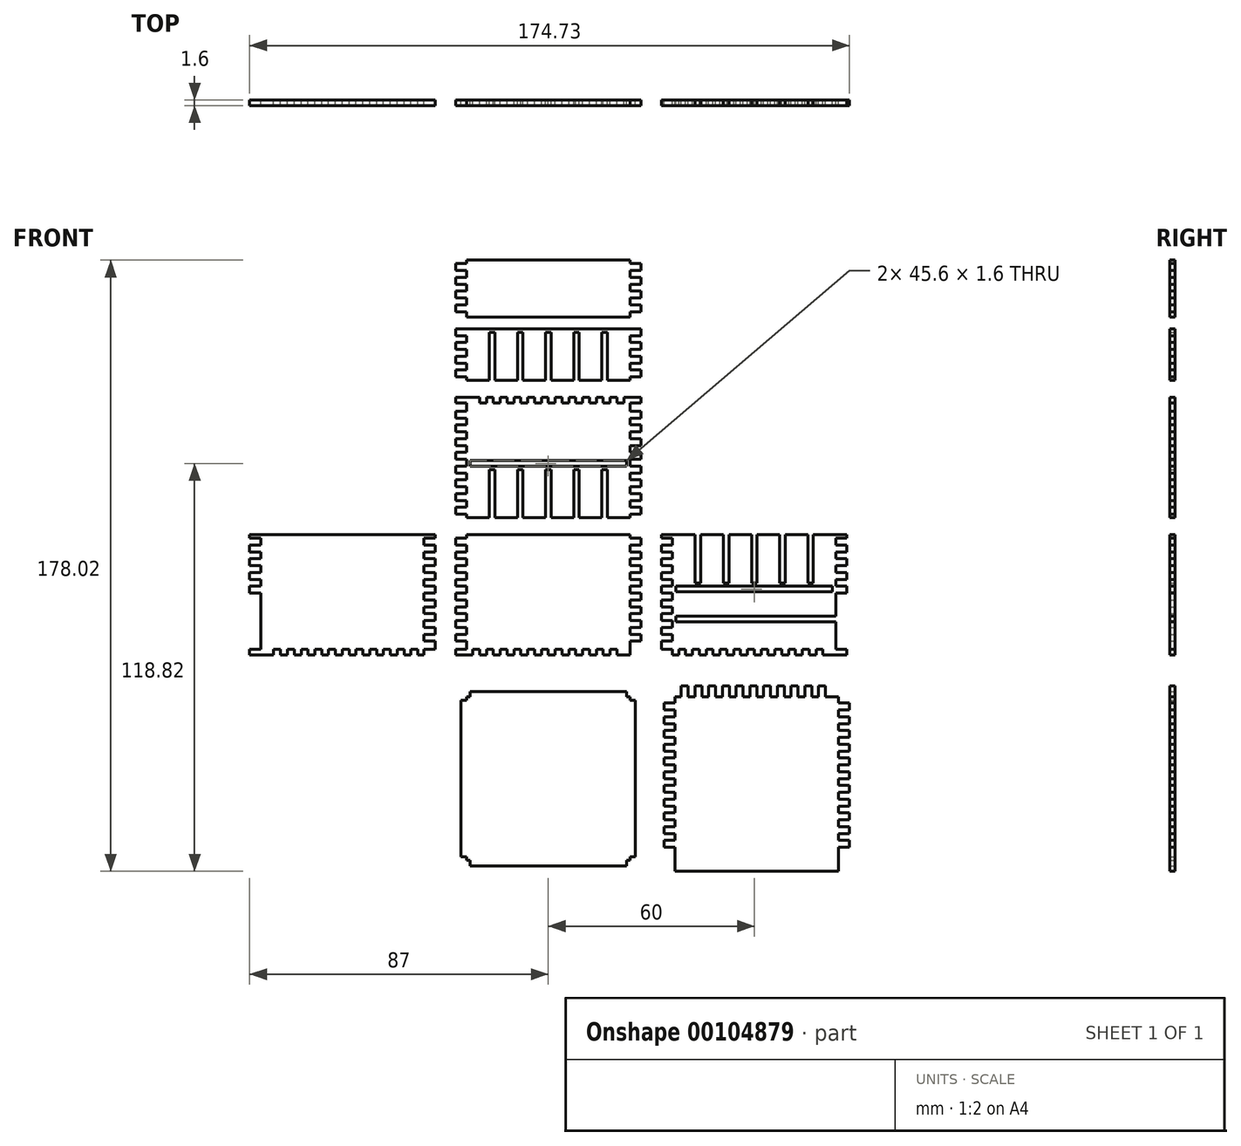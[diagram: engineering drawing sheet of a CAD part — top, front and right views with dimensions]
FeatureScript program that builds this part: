
annotation { "Feature Type Name" : "Feature", "Feature Type Description" : "" }
export const myFeature = defineFeature(function(context is Context, id is Id, definition is map)
    precondition{}
    {
        {
            var Q0;
            Q0=qCreatedBy(makeId("Front.planeOp"),FACE);
            var sketch = newSketch(context, id + "F0", { "sketchPlane" : qUnion([Q0])});
            skLineSegment(sketch, "E0", {"start": v(0, 17.5) * mm, "end": v(27, 17.5) * mm});
            skLineSegment(sketch, "E1", {"start": v(27, 17.5) * mm, "end": v(27, -17.5) * mm});
            skLineSegment(sketch, "E2", {"start": v(27, -17.5) * mm, "end": v(0, -17.5) * mm});
            skLineSegment(sketch, "E3", {"start": v(23.8, 17.5) * mm, "end": v(23.8, -17.5) * mm});
            skLineSegment(sketch, "E4", {"start": v(23.8, 16.5) * mm, "end": v(27, 16.5) * mm});
            skLineSegment(sketch, "E5", {"start": v(23.8, 14.5) * mm, "end": v(27, 14.5) * mm});
            skLineSegment(sketch, "E6.1.0.0", {"start": v(23.8, 12.5) * mm, "end": v(27, 12.5) * mm});
            skLineSegment(sketch, "E6.1.0.1", {"start": v(23.8, 10.5) * mm, "end": v(27, 10.5) * mm});
            skLineSegment(sketch, "E6.2.0.0", {"start": v(23.8, 8.5) * mm, "end": v(27, 8.5) * mm});
            skLineSegment(sketch, "E6.2.0.1", {"start": v(23.8, 6.5) * mm, "end": v(27, 6.5) * mm});
            skLineSegment(sketch, "E6.3.0.0", {"start": v(23.8, 4.5) * mm, "end": v(27, 4.5) * mm});
            skLineSegment(sketch, "E6.3.0.1", {"start": v(23.8, 2.5) * mm, "end": v(27, 2.5) * mm});
            skLineSegment(sketch, "E6.4.0.0", {"start": v(23.8, 0.5) * mm, "end": v(27, 0.5) * mm});
            skLineSegment(sketch, "E6.4.0.1", {"start": v(23.8, -1.5) * mm, "end": v(27, -1.5) * mm});
            skLineSegment(sketch, "E6.5.0.0", {"start": v(23.8, -3.5) * mm, "end": v(27, -3.5) * mm});
            skLineSegment(sketch, "E6.5.0.1", {"start": v(23.8, -5.5) * mm, "end": v(27, -5.5) * mm});
            skLineSegment(sketch, "E6.6.0.0", {"start": v(23.8, -7.5) * mm, "end": v(27, -7.5) * mm});
            skLineSegment(sketch, "E6.6.0.1", {"start": v(23.8, -9.5) * mm, "end": v(27, -9.5) * mm});
            skLineSegment(sketch, "E6.7.0.0", {"start": v(23.8, -11.5) * mm, "end": v(27, -11.5) * mm});
            skLineSegment(sketch, "E6.7.0.1", {"start": v(23.8, -13.5) * mm, "end": v(27, -13.5) * mm});
            skLineSegment(sketch, "E6.8.0.1", {"start": v(23.8, -17.5) * mm, "end": v(27, -17.5) * mm});
            skLineSegment(sketch, "E6.direction1", {"start": v(23.8, 16.5) * mm, "end": v(23.8, 12.5) * mm, "construction": true});
            skLineSegment(sketch, "E7.MirrorCS", {"start": v(0, 17.5) * mm, "end": v(-27, 17.5) * mm});
            skLineSegment(sketch, "E8.MirrorCS", {"start": v(-23.8, 16.5) * mm, "end": v(-27, 16.5) * mm});
            skLineSegment(sketch, "E9.MirrorCS", {"start": v(-23.8, 14.5) * mm, "end": v(-27, 14.5) * mm});
            skLineSegment(sketch, "E10.MirrorCS", {"start": v(-23.8, 12.5) * mm, "end": v(-27, 12.5) * mm});
            skLineSegment(sketch, "E11.MirrorCS", {"start": v(-23.8, 10.5) * mm, "end": v(-27, 10.5) * mm});
            skLineSegment(sketch, "E12.MirrorCS", {"start": v(-23.8, 8.5) * mm, "end": v(-27, 8.5) * mm});
            skLineSegment(sketch, "E13.MirrorCS", {"start": v(-23.8, 6.5) * mm, "end": v(-27, 6.5) * mm});
            skLineSegment(sketch, "E14.MirrorCS", {"start": v(-23.8, 4.5) * mm, "end": v(-27, 4.5) * mm});
            skLineSegment(sketch, "E15.MirrorCS", {"start": v(-23.8, 2.5) * mm, "end": v(-27, 2.5) * mm});
            skLineSegment(sketch, "E16.MirrorCS", {"start": v(-23.8, 0.5) * mm, "end": v(-27, 0.5) * mm});
            skLineSegment(sketch, "E17.MirrorCS", {"start": v(-23.8, -1.5) * mm, "end": v(-27, -1.5) * mm});
            skLineSegment(sketch, "E18.MirrorCS", {"start": v(-23.8, -5.5) * mm, "end": v(-27, -5.5) * mm});
            skLineSegment(sketch, "E19.MirrorCS", {"start": v(-23.8, -3.5) * mm, "end": v(-27, -3.5) * mm});
            skLineSegment(sketch, "E20.MirrorCS", {"start": v(-23.8, -7.5) * mm, "end": v(-27, -7.5) * mm});
            skLineSegment(sketch, "E21.MirrorCS", {"start": v(-23.8, -9.5) * mm, "end": v(-27, -9.5) * mm});
            skLineSegment(sketch, "E22.MirrorCS", {"start": v(-23.8, -11.5) * mm, "end": v(-27, -11.5) * mm});
            skLineSegment(sketch, "E23.MirrorCS", {"start": v(-23.8, -13.5) * mm, "end": v(-27, -13.5) * mm});
            skLineSegment(sketch, "E24.MirrorCS", {"start": v(-23.8, -17.5) * mm, "end": v(-27, -17.5) * mm});
            skLineSegment(sketch, "E25.MirrorCS", {"start": v(-27, -17.5) * mm, "end": v(0, -17.5) * mm});
            skLineSegment(sketch, "E26.MirrorCS", {"start": v(-23.8, 17.5) * mm, "end": v(-23.8, -17.5) * mm});
            skLineSegment(sketch, "E27.MirrorCS", {"start": v(-27, 17.5) * mm, "end": v(-27, -17.5) * mm});
            skLineSegment(sketch, "E28.1", {"start": v(-30, 20) * mm, "end": v(-30, -20) * mm, "construction": true});
            skLineSegment(sketch, "E28.5", {"start": v(30, 20) * mm, "end": v(30, -20) * mm, "construction": true});
            skLineSegment(sketch, "E29", {"start": v(-30, 20) * mm, "end": v(30, 20) * mm, "construction": true});
            skLineSegment(sketch, "E30", {"start": v(30, -20) * mm, "end": v(-30, -20) * mm, "construction": true});
            skLineSegment(sketch, "E31.MirrorCS", {"start": v(-0.8, 22.5) * mm, "end": v(-7.4, 22.5) * mm});
            skLineSegment(sketch, "E32.MirrorCS", {"start": v(0.8, 22.5) * mm, "end": v(7.4, 22.5) * mm});
            skLineSegment(sketch, "E33.MirrorCS", {"start": v(23.8, 23.5) * mm, "end": v(27, 23.5) * mm});
            skLineSegment(sketch, "E34.MirrorCS", {"start": v(23.8, 25.5) * mm, "end": v(27, 25.5) * mm});
            skLineSegment(sketch, "E35.MirrorCS", {"start": v(23.8, 27.5) * mm, "end": v(27, 27.5) * mm});
            skLineSegment(sketch, "E36.MirrorCS", {"start": v(23.8, 29.5) * mm, "end": v(27, 29.5) * mm});
            skLineSegment(sketch, "E37.MirrorCS", {"start": v(23.8, 31.5) * mm, "end": v(27, 31.5) * mm});
            skLineSegment(sketch, "E38.MirrorCS", {"start": v(23.8, 33.5) * mm, "end": v(27, 33.5) * mm});
            skLineSegment(sketch, "E39.MirrorCS", {"start": v(23.8, 35.5) * mm, "end": v(27, 35.5) * mm});
            skLineSegment(sketch, "E40.MirrorCS", {"start": v(23.8, 37.5) * mm, "end": v(27, 37.5) * mm});
            skLineSegment(sketch, "E41.MirrorCS", {"start": v(23.8, 39.5) * mm, "end": v(27, 39.5) * mm});
            skLineSegment(sketch, "E42.MirrorCS", {"start": v(23.8, 43.5) * mm, "end": v(27, 43.5) * mm});
            skLineSegment(sketch, "E43.MirrorCS", {"start": v(23.8, 45.5) * mm, "end": v(27, 45.5) * mm});
            skLineSegment(sketch, "E44.MirrorCS", {"start": v(23.8, 47.5) * mm, "end": v(27, 47.5) * mm});
            skLineSegment(sketch, "E45.MirrorCS", {"start": v(23.8, 49.5) * mm, "end": v(27, 49.5) * mm});
            skLineSegment(sketch, "E46.MirrorCS", {"start": v(23.8, 51.5) * mm, "end": v(27, 51.5) * mm});
            skLineSegment(sketch, "E47.MirrorCS", {"start": v(23.8, 53.5) * mm, "end": v(27, 53.5) * mm});
            skLineSegment(sketch, "E48.MirrorCS", {"start": v(27, 57.5) * mm, "end": v(0, 57.5) * mm});
            skLineSegment(sketch, "E49.MirrorCS", {"start": v(-27, 57.5) * mm, "end": v(0, 57.5) * mm});
            skLineSegment(sketch, "E50.MirrorCS", {"start": v(-23.8, 53.5) * mm, "end": v(-27, 53.5) * mm});
            skLineSegment(sketch, "E51.MirrorCS", {"start": v(-23.8, 51.5) * mm, "end": v(-27, 51.5) * mm});
            skLineSegment(sketch, "E52.MirrorCS", {"start": v(-23.8, 49.5) * mm, "end": v(-27, 49.5) * mm});
            skLineSegment(sketch, "E53.MirrorCS", {"start": v(-23.8, 47.5) * mm, "end": v(-27, 47.5) * mm});
            skLineSegment(sketch, "E54.MirrorCS", {"start": v(-23.8, 45.5) * mm, "end": v(-27, 45.5) * mm});
            skLineSegment(sketch, "E55.MirrorCS", {"start": v(-23.8, 43.5) * mm, "end": v(-27, 43.5) * mm});
            skLineSegment(sketch, "E56.MirrorCS", {"start": v(-23.8, 39.5) * mm, "end": v(-27, 39.5) * mm});
            skLineSegment(sketch, "E57.MirrorCS", {"start": v(-23.8, 37.5) * mm, "end": v(-27, 37.5) * mm});
            skLineSegment(sketch, "E58.MirrorCS", {"start": v(-23.8, 35.5) * mm, "end": v(-27, 35.5) * mm});
            skLineSegment(sketch, "E59.MirrorCS", {"start": v(-23.8, 33.5) * mm, "end": v(-27, 33.5) * mm});
            skLineSegment(sketch, "E60.MirrorCS", {"start": v(-23.8, 31.5) * mm, "end": v(-27, 31.5) * mm});
            skLineSegment(sketch, "E61.MirrorCS", {"start": v(-23.8, 29.5) * mm, "end": v(-27, 29.5) * mm});
            skLineSegment(sketch, "E62.MirrorCS", {"start": v(-23.8, 27.5) * mm, "end": v(-27, 27.5) * mm});
            skLineSegment(sketch, "E63.MirrorCS", {"start": v(-23.8, 25.5) * mm, "end": v(-27, 25.5) * mm});
            skLineSegment(sketch, "E64.MirrorCS", {"start": v(-23.8, 23.5) * mm, "end": v(-27, 23.5) * mm});
            skLineSegment(sketch, "E65.MirrorCS", {"start": v(-27, 22.5) * mm, "end": v(-27, 57.5) * mm});
            skLineSegment(sketch, "E66.MirrorCS", {"start": v(-23.8, 22.5) * mm, "end": v(-23.8, 57.5) * mm});
            skLineSegment(sketch, "E67.MirrorCS", {"start": v(23.8, 22.5) * mm, "end": v(23.8, 57.5) * mm});
            skLineSegment(sketch, "E68.MirrorCS", {"start": v(27, 22.5) * mm, "end": v(27, 57.5) * mm});
            skLineSegment(sketch, "E69.MirrorCS", {"start": v(-60, 17.5) * mm, "end": v(-33, 17.5) * mm});
            skLineSegment(sketch, "E70.MirrorCS", {"start": v(-60, 17.5) * mm, "end": v(-87, 17.5) * mm});
            skLineSegment(sketch, "E71.MirrorCS", {"start": v(-33, -17.5) * mm, "end": v(-60, -17.5) * mm});
            skLineSegment(sketch, "E72.MirrorCS", {"start": v(-87, -17.5) * mm, "end": v(-60, -17.5) * mm});
            skLineSegment(sketch, "E73.MirrorCS", {"start": v(-36.2, -13.5) * mm, "end": v(-33, -13.5) * mm});
            skLineSegment(sketch, "E74.MirrorCS", {"start": v(-36.2, -11.5) * mm, "end": v(-33, -11.5) * mm});
            skLineSegment(sketch, "E75.MirrorCS", {"start": v(-36.2, -9.5) * mm, "end": v(-33, -9.5) * mm});
            skLineSegment(sketch, "E76.MirrorCS", {"start": v(-36.2, -7.5) * mm, "end": v(-33, -7.5) * mm});
            skLineSegment(sketch, "E77.MirrorCS", {"start": v(-36.2, -5.5) * mm, "end": v(-33, -5.5) * mm});
            skLineSegment(sketch, "E78.MirrorCS", {"start": v(-36.2, -3.5) * mm, "end": v(-33, -3.5) * mm});
            skLineSegment(sketch, "E79.MirrorCS", {"start": v(-36.2, -1.5) * mm, "end": v(-33, -1.5) * mm});
            skLineSegment(sketch, "E80.MirrorCS", {"start": v(-36.2, 0.5) * mm, "end": v(-33, 0.5) * mm});
            skLineSegment(sketch, "E81.MirrorCS", {"start": v(-36.2, 2.5) * mm, "end": v(-33, 2.5) * mm});
            skLineSegment(sketch, "E82.MirrorCS", {"start": v(-36.2, 4.5) * mm, "end": v(-33, 4.5) * mm});
            skLineSegment(sketch, "E83.MirrorCS", {"start": v(-36.2, 6.5) * mm, "end": v(-33, 6.5) * mm});
            skLineSegment(sketch, "E84.MirrorCS", {"start": v(-36.2, 8.5) * mm, "end": v(-33, 8.5) * mm});
            skLineSegment(sketch, "E85.MirrorCS", {"start": v(-36.2, 10.5) * mm, "end": v(-33, 10.5) * mm});
            skLineSegment(sketch, "E86.MirrorCS", {"start": v(-36.2, 12.5) * mm, "end": v(-33, 12.5) * mm});
            skLineSegment(sketch, "E87.MirrorCS", {"start": v(-36.2, 14.5) * mm, "end": v(-33, 14.5) * mm});
            skLineSegment(sketch, "E88.MirrorCS", {"start": v(-36.2, 16.5) * mm, "end": v(-33, 16.5) * mm});
            skLineSegment(sketch, "E89.MirrorCS", {"start": v(-36.2, 17.5) * mm, "end": v(-36.2, -17.5) * mm});
            skLineSegment(sketch, "E90.MirrorCS", {"start": v(-33, 17.5) * mm, "end": v(-33, -17.5) * mm});
            skLineSegment(sketch, "E91.MirrorCS", {"start": v(-83.8, 17.5) * mm, "end": v(-83.8, -17.5) * mm});
            skLineSegment(sketch, "E92.MirrorCS", {"start": v(-87, 17.5) * mm, "end": v(-87, -17.5) * mm});
            skLineSegment(sketch, "E93.MirrorCS", {"start": v(-83.8, 16.5) * mm, "end": v(-87, 16.5) * mm});
            skLineSegment(sketch, "E94.MirrorCS", {"start": v(-83.8, 14.5) * mm, "end": v(-87, 14.5) * mm});
            skLineSegment(sketch, "E95.MirrorCS", {"start": v(-83.8, 12.5) * mm, "end": v(-87, 12.5) * mm});
            skLineSegment(sketch, "E96.MirrorCS", {"start": v(-83.8, 10.5) * mm, "end": v(-87, 10.5) * mm});
            skLineSegment(sketch, "E97.MirrorCS", {"start": v(-83.8, 8.5) * mm, "end": v(-87, 8.5) * mm});
            skLineSegment(sketch, "E98.MirrorCS", {"start": v(-83.8, 6.5) * mm, "end": v(-87, 6.5) * mm});
            skLineSegment(sketch, "E99.MirrorCS", {"start": v(-83.8, 4.5) * mm, "end": v(-87, 4.5) * mm});
            skLineSegment(sketch, "E100.MirrorCS", {"start": v(-83.8, 2.5) * mm, "end": v(-87, 2.5) * mm});
            skLineSegment(sketch, "E101.MirrorCS", {"start": v(-83.8, 0.5) * mm, "end": v(-87, 0.5) * mm});
            skLineSegment(sketch, "E102.MirrorCS", {"start": v(30, 60) * mm, "end": v(-30, 60) * mm, "construction": true});
            skLineSegment(sketch, "E103.MirrorCS", {"start": v(27, 62.5) * mm, "end": v(17.2, 62.5) * mm});
            skLineSegment(sketch, "E104.MirrorCS", {"start": v(-27, 62.5) * mm, "end": v(-17.2, 62.5) * mm});
            skLineSegment(sketch, "E105.MirrorCS", {"start": v(0, 97.5) * mm, "end": v(-27, 97.5) * mm});
            skLineSegment(sketch, "E106.MirrorCS", {"start": v(0, 97.5) * mm, "end": v(27, 97.5) * mm});
            skLineSegment(sketch, "E107.MirrorCS", {"start": v(-23.8, 96.5) * mm, "end": v(-27, 96.5) * mm});
            skLineSegment(sketch, "E108.MirrorCS", {"start": v(-23.8, 94.5) * mm, "end": v(-27, 94.5) * mm});
            skLineSegment(sketch, "E109.MirrorCS", {"start": v(-23.8, 92.5) * mm, "end": v(-27, 92.5) * mm});
            skLineSegment(sketch, "E110.MirrorCS", {"start": v(-23.8, 90.5) * mm, "end": v(-27, 90.5) * mm});
            skLineSegment(sketch, "E111.MirrorCS", {"start": v(-23.8, 88.5) * mm, "end": v(-27, 88.5) * mm});
            skLineSegment(sketch, "E112.MirrorCS", {"start": v(-23.8, 86.5) * mm, "end": v(-27, 86.5) * mm});
            skLineSegment(sketch, "E113.MirrorCS", {"start": v(-23.8, 84.5) * mm, "end": v(-27, 84.5) * mm});
            skLineSegment(sketch, "E114.MirrorCS", {"start": v(-23.8, 82.5) * mm, "end": v(-27, 82.5) * mm});
            skLineSegment(sketch, "E115.MirrorCS", {"start": v(23.8, 82.5) * mm, "end": v(27, 82.5) * mm});
            skLineSegment(sketch, "E116.MirrorCS", {"start": v(23.8, 84.5) * mm, "end": v(27, 84.5) * mm});
            skLineSegment(sketch, "E117.MirrorCS", {"start": v(23.8, 96.5) * mm, "end": v(27, 96.5) * mm});
            skLineSegment(sketch, "E118.MirrorCS", {"start": v(23.8, 94.5) * mm, "end": v(27, 94.5) * mm});
            skLineSegment(sketch, "E119.MirrorCS", {"start": v(23.8, 92.5) * mm, "end": v(27, 92.5) * mm});
            skLineSegment(sketch, "E120.MirrorCS", {"start": v(23.8, 90.5) * mm, "end": v(27, 90.5) * mm});
            skLineSegment(sketch, "E121.MirrorCS", {"start": v(23.8, 88.5) * mm, "end": v(27, 88.5) * mm});
            skLineSegment(sketch, "E122.MirrorCS", {"start": v(23.8, 86.5) * mm, "end": v(27, 86.5) * mm});
            skLineSegment(sketch, "E123.MirrorCS", {"start": v(23.8, 97.5) * mm, "end": v(23.8, 82.5) * mm});
            skLineSegment(sketch, "E124.MirrorCS", {"start": v(27, 97.5) * mm, "end": v(27, 82.5) * mm});
            skLineSegment(sketch, "E125.MirrorCS", {"start": v(-23.8, 97.5) * mm, "end": v(-23.8, 82.5) * mm});
            skLineSegment(sketch, "E126.MirrorCS", {"start": v(-27, 97.5) * mm, "end": v(-27, 82.5) * mm});
            skLineSegment(sketch, "E127", {"start": v(0, -15.9) * mm, "end": v(22, -15.9) * mm});
            skLineSegment(sketch, "E128", {"start": v(22, -15.9) * mm, "end": v(22, -17.5) * mm});
            skLineSegment(sketch, "E129", {"start": v(20, -15.9) * mm, "end": v(20, -17.5) * mm});
            skLineSegment(sketch, "E130.MirrorCS", {"start": v(0, -15.9) * mm, "end": v(-22, -15.9) * mm});
            skLineSegment(sketch, "E131.MirrorCS", {"start": v(-22, -15.9) * mm, "end": v(-22, -17.5) * mm});
            skLineSegment(sketch, "E132.MirrorCS", {"start": v(-20, -15.9) * mm, "end": v(-20, -17.5) * mm});
            skLineSegment(sketch, "E133.1.0.0", {"start": v(16, -15.9) * mm, "end": v(16, -17.5) * mm});
            skLineSegment(sketch, "E133.1.0.1", {"start": v(18, -15.9) * mm, "end": v(18, -17.5) * mm});
            skLineSegment(sketch, "E133.2.0.0", {"start": v(12, -15.9) * mm, "end": v(12, -17.5) * mm});
            skLineSegment(sketch, "E133.2.0.1", {"start": v(14, -15.9) * mm, "end": v(14, -17.5) * mm});
            skLineSegment(sketch, "E133.3.0.0", {"start": v(8, -15.9) * mm, "end": v(8, -17.5) * mm});
            skLineSegment(sketch, "E133.3.0.1", {"start": v(10, -15.9) * mm, "end": v(10, -17.5) * mm});
            skLineSegment(sketch, "E133.4.0.0", {"start": v(4, -15.9) * mm, "end": v(4, -17.5) * mm});
            skLineSegment(sketch, "E133.4.0.1", {"start": v(6, -15.9) * mm, "end": v(6, -17.5) * mm});
            skLineSegment(sketch, "E133.5.0.1", {"start": v(2, -15.9) * mm, "end": v(2, -17.5) * mm});
            skLineSegment(sketch, "E133.direction1", {"start": v(20, -17.5) * mm, "end": v(16, -17.5) * mm, "construction": true});
            skLineSegment(sketch, "E134.1.0.0", {"start": v(-16, -15.9) * mm, "end": v(-16, -17.5) * mm});
            skLineSegment(sketch, "E134.1.0.1", {"start": v(-18, -15.9) * mm, "end": v(-18, -17.5) * mm});
            skLineSegment(sketch, "E134.2.0.0", {"start": v(-12, -15.9) * mm, "end": v(-12, -17.5) * mm});
            skLineSegment(sketch, "E134.2.0.1", {"start": v(-14, -15.9) * mm, "end": v(-14, -17.5) * mm});
            skLineSegment(sketch, "E134.3.0.0", {"start": v(-8, -15.9) * mm, "end": v(-8, -17.5) * mm});
            skLineSegment(sketch, "E134.3.0.1", {"start": v(-10, -15.9) * mm, "end": v(-10, -17.5) * mm});
            skLineSegment(sketch, "E134.4.0.0", {"start": v(-4, -15.9) * mm, "end": v(-4, -17.5) * mm});
            skLineSegment(sketch, "E134.4.0.1", {"start": v(-6, -15.9) * mm, "end": v(-6, -17.5) * mm});
            skLineSegment(sketch, "E134.5.0.1", {"start": v(-2, -15.9) * mm, "end": v(-2, -17.5) * mm});
            skLineSegment(sketch, "E134.direction1", {"start": v(-22, -17.5) * mm, "end": v(-18, -17.5) * mm, "construction": true});
            skLineSegment(sketch, "E135", {"start": v(0, -15.9) * mm, "end": v(0, -17.5) * mm});
            skLineSegment(sketch, "E136.MirrorCS", {"start": v(59.2, 17.5) * mm, "end": v(52.6, 17.5) * mm});
            skLineSegment(sketch, "E137.MirrorCS", {"start": v(60.8, 17.5) * mm, "end": v(67.4, 17.5) * mm});
            skLineSegment(sketch, "E138.MirrorCS", {"start": v(33, 17.5) * mm, "end": v(33, -17.5) * mm});
            skLineSegment(sketch, "E139.MirrorCS", {"start": v(36.2, 17.5) * mm, "end": v(36.2, -17.5) * mm});
            skLineSegment(sketch, "E140.MirrorCS", {"start": v(83.8, 17.5) * mm, "end": v(83.8, -6.2) * mm});
            skLineSegment(sketch, "E141.MirrorCS", {"start": v(87, 17.5) * mm, "end": v(87, -17.5) * mm});
            skLineSegment(sketch, "E142.MirrorCS", {"start": v(36.2, 16.5) * mm, "end": v(33, 16.5) * mm});
            skLineSegment(sketch, "E143.MirrorCS", {"start": v(36.2, 14.5) * mm, "end": v(33, 14.5) * mm});
            skLineSegment(sketch, "E144.MirrorCS", {"start": v(36.2, 12.5) * mm, "end": v(33, 12.5) * mm});
            skLineSegment(sketch, "E145.MirrorCS", {"start": v(36.2, 10.5) * mm, "end": v(33, 10.5) * mm});
            skLineSegment(sketch, "E146.MirrorCS", {"start": v(36.2, 8.5) * mm, "end": v(33, 8.5) * mm});
            skLineSegment(sketch, "E147.MirrorCS", {"start": v(36.2, 6.5) * mm, "end": v(33, 6.5) * mm});
            skLineSegment(sketch, "E148.MirrorCS", {"start": v(36.2, 4.5) * mm, "end": v(33, 4.5) * mm});
            skLineSegment(sketch, "E149.MirrorCS", {"start": v(36.2, 2.5) * mm, "end": v(33, 2.5) * mm});
            skLineSegment(sketch, "E150.MirrorCS", {"start": v(36.2, 0.5) * mm, "end": v(33, 0.5) * mm});
            skLineSegment(sketch, "E151.MirrorCS", {"start": v(36.2, -1.5) * mm, "end": v(33, -1.5) * mm});
            skLineSegment(sketch, "E152.MirrorCS", {"start": v(36.2, -3.5) * mm, "end": v(33, -3.5) * mm});
            skLineSegment(sketch, "E153.MirrorCS", {"start": v(36.2, -5.5) * mm, "end": v(33, -5.5) * mm});
            skLineSegment(sketch, "E154.MirrorCS", {"start": v(36.2, -7.5) * mm, "end": v(33, -7.5) * mm});
            skLineSegment(sketch, "E155.MirrorCS", {"start": v(36.2, -9.5) * mm, "end": v(33, -9.5) * mm});
            skLineSegment(sketch, "E156.MirrorCS", {"start": v(36.2, -11.5) * mm, "end": v(33, -11.5) * mm});
            skLineSegment(sketch, "E157.MirrorCS", {"start": v(36.2, -13.5) * mm, "end": v(33, -13.5) * mm});
            skLineSegment(sketch, "E158.MirrorCS", {"start": v(83.8, 0.5) * mm, "end": v(87, 0.5) * mm});
            skLineSegment(sketch, "E159.MirrorCS", {"start": v(83.8, 2.5) * mm, "end": v(87, 2.5) * mm});
            skLineSegment(sketch, "E160.MirrorCS", {"start": v(83.8, 4.5) * mm, "end": v(87, 4.5) * mm});
            skLineSegment(sketch, "E161.MirrorCS", {"start": v(83.8, 6.5) * mm, "end": v(87, 6.5) * mm});
            skLineSegment(sketch, "E162.MirrorCS", {"start": v(83.8, 8.5) * mm, "end": v(87, 8.5) * mm});
            skLineSegment(sketch, "E163.MirrorCS", {"start": v(83.8, 10.5) * mm, "end": v(87, 10.5) * mm});
            skLineSegment(sketch, "E164.MirrorCS", {"start": v(83.8, 12.5) * mm, "end": v(87, 12.5) * mm});
            skLineSegment(sketch, "E165.MirrorCS", {"start": v(83.8, 14.5) * mm, "end": v(87, 14.5) * mm});
            skLineSegment(sketch, "E166.MirrorCS", {"start": v(83.8, 16.5) * mm, "end": v(87, 16.5) * mm});
            skLineSegment(sketch, "E167.MirrorCS", {"start": v(60, -15.9) * mm, "end": v(82, -15.9) * mm});
            skLineSegment(sketch, "E168.MirrorCS", {"start": v(60, -15.9) * mm, "end": v(38, -15.9) * mm});
            skLineSegment(sketch, "E169.MirrorCS", {"start": v(87, -17.5) * mm, "end": v(60, -17.5) * mm});
            skLineSegment(sketch, "E170.MirrorCS", {"start": v(33, -17.5) * mm, "end": v(60, -17.5) * mm});
            skLineSegment(sketch, "E171.MirrorCS", {"start": v(38, -15.9) * mm, "end": v(38, -17.5) * mm});
            skLineSegment(sketch, "E172.MirrorCS", {"start": v(40, -15.9) * mm, "end": v(40, -17.5) * mm});
            skLineSegment(sketch, "E173.MirrorCS", {"start": v(42, -15.9) * mm, "end": v(42, -17.5) * mm});
            skLineSegment(sketch, "E174.MirrorCS", {"start": v(44, -15.9) * mm, "end": v(44, -17.5) * mm});
            skLineSegment(sketch, "E175.MirrorCS", {"start": v(46, -15.9) * mm, "end": v(46, -17.5) * mm});
            skLineSegment(sketch, "E176.MirrorCS", {"start": v(48, -15.9) * mm, "end": v(48, -17.5) * mm});
            skLineSegment(sketch, "E177.MirrorCS", {"start": v(50, -15.9) * mm, "end": v(50, -17.5) * mm});
            skLineSegment(sketch, "E178.MirrorCS", {"start": v(52, -15.9) * mm, "end": v(52, -17.5) * mm});
            skLineSegment(sketch, "E179.MirrorCS", {"start": v(54, -15.9) * mm, "end": v(54, -17.5) * mm});
            skLineSegment(sketch, "E180.MirrorCS", {"start": v(56, -15.9) * mm, "end": v(56, -17.5) * mm});
            skLineSegment(sketch, "E181.MirrorCS", {"start": v(58, -15.9) * mm, "end": v(58, -17.5) * mm});
            skLineSegment(sketch, "E182.MirrorCS", {"start": v(60, -15.9) * mm, "end": v(60, -17.5) * mm});
            skLineSegment(sketch, "E183.MirrorCS", {"start": v(62, -15.9) * mm, "end": v(62, -17.5) * mm});
            skLineSegment(sketch, "E184.MirrorCS", {"start": v(64, -15.9) * mm, "end": v(64, -17.5) * mm});
            skLineSegment(sketch, "E185.MirrorCS", {"start": v(66, -15.9) * mm, "end": v(66, -17.5) * mm});
            skLineSegment(sketch, "E186.MirrorCS", {"start": v(68, -15.9) * mm, "end": v(68, -17.5) * mm});
            skLineSegment(sketch, "E187.MirrorCS", {"start": v(70, -15.9) * mm, "end": v(70, -17.5) * mm});
            skLineSegment(sketch, "E188.MirrorCS", {"start": v(72, -15.9) * mm, "end": v(72, -17.5) * mm});
            skLineSegment(sketch, "E189.MirrorCS", {"start": v(74, -15.9) * mm, "end": v(74, -17.5) * mm});
            skLineSegment(sketch, "E190.MirrorCS", {"start": v(76, -15.9) * mm, "end": v(76, -17.5) * mm});
            skLineSegment(sketch, "E191.MirrorCS", {"start": v(78, -15.9) * mm, "end": v(78, -17.5) * mm});
            skLineSegment(sketch, "E192.MirrorCS", {"start": v(80, -15.9) * mm, "end": v(80, -17.5) * mm});
            skLineSegment(sketch, "E193.MirrorCS", {"start": v(82, -15.9) * mm, "end": v(82, -17.5) * mm});
            skLineSegment(sketch, "E194.MirrorCS", {"start": v(-60, -15.9) * mm, "end": v(-38, -15.9) * mm});
            skLineSegment(sketch, "E195.MirrorCS", {"start": v(-60, -15.9) * mm, "end": v(-82, -15.9) * mm});
            skLineSegment(sketch, "E196.MirrorCS", {"start": v(-38, -15.9) * mm, "end": v(-38, -17.5) * mm});
            skLineSegment(sketch, "E197.MirrorCS", {"start": v(-40, -15.9) * mm, "end": v(-40, -17.5) * mm});
            skLineSegment(sketch, "E198.MirrorCS", {"start": v(-42, -15.9) * mm, "end": v(-42, -17.5) * mm});
            skLineSegment(sketch, "E199.MirrorCS", {"start": v(-44, -15.9) * mm, "end": v(-44, -17.5) * mm});
            skLineSegment(sketch, "E200.MirrorCS", {"start": v(-46, -15.9) * mm, "end": v(-46, -17.5) * mm});
            skLineSegment(sketch, "E201.MirrorCS", {"start": v(-48, -15.9) * mm, "end": v(-48, -17.5) * mm});
            skLineSegment(sketch, "E202.MirrorCS", {"start": v(-50, -15.9) * mm, "end": v(-50, -17.5) * mm});
            skLineSegment(sketch, "E203.MirrorCS", {"start": v(-52, -15.9) * mm, "end": v(-52, -17.5) * mm});
            skLineSegment(sketch, "E204.MirrorCS", {"start": v(-54, -15.9) * mm, "end": v(-54, -17.5) * mm});
            skLineSegment(sketch, "E205.MirrorCS", {"start": v(-56, -15.9) * mm, "end": v(-56, -17.5) * mm});
            skLineSegment(sketch, "E206.MirrorCS", {"start": v(-58, -15.9) * mm, "end": v(-58, -17.5) * mm});
            skLineSegment(sketch, "E207.MirrorCS", {"start": v(-60, -15.9) * mm, "end": v(-60, -17.5) * mm});
            skLineSegment(sketch, "E208.MirrorCS", {"start": v(-62, -15.9) * mm, "end": v(-62, -17.5) * mm});
            skLineSegment(sketch, "E209.MirrorCS", {"start": v(-64, -15.9) * mm, "end": v(-64, -17.5) * mm});
            skLineSegment(sketch, "E210.MirrorCS", {"start": v(-82, -15.9) * mm, "end": v(-82, -17.5) * mm});
            skLineSegment(sketch, "E211.MirrorCS", {"start": v(-80, -15.9) * mm, "end": v(-80, -17.5) * mm});
            skLineSegment(sketch, "E212.MirrorCS", {"start": v(-78, -15.9) * mm, "end": v(-78, -17.5) * mm});
            skLineSegment(sketch, "E213.MirrorCS", {"start": v(-76, -15.9) * mm, "end": v(-76, -17.5) * mm});
            skLineSegment(sketch, "E214.MirrorCS", {"start": v(-74, -15.9) * mm, "end": v(-74, -17.5) * mm});
            skLineSegment(sketch, "E215.MirrorCS", {"start": v(-72, -15.9) * mm, "end": v(-72, -17.5) * mm});
            skLineSegment(sketch, "E216.MirrorCS", {"start": v(-70, -15.9) * mm, "end": v(-70, -17.5) * mm});
            skLineSegment(sketch, "E217.MirrorCS", {"start": v(-66, -15.9) * mm, "end": v(-66, -17.5) * mm});
            skLineSegment(sketch, "E218.MirrorCS", {"start": v(-68, -15.9) * mm, "end": v(-68, -17.5) * mm});
            skLineSegment(sketch, "E219.MirrorCS", {"start": v(0, 55.9) * mm, "end": v(-22, 55.9) * mm});
            skLineSegment(sketch, "E220.MirrorCS", {"start": v(0, 55.9) * mm, "end": v(22, 55.9) * mm});
            skLineSegment(sketch, "E221.MirrorCS", {"start": v(-22, 55.9) * mm, "end": v(-22, 57.5) * mm});
            skLineSegment(sketch, "E222.MirrorCS", {"start": v(-20, 55.9) * mm, "end": v(-20, 57.5) * mm});
            skLineSegment(sketch, "E223.MirrorCS", {"start": v(-18, 55.9) * mm, "end": v(-18, 57.5) * mm});
            skLineSegment(sketch, "E224.MirrorCS", {"start": v(-16, 55.9) * mm, "end": v(-16, 57.5) * mm});
            skLineSegment(sketch, "E225.MirrorCS", {"start": v(-14, 55.9) * mm, "end": v(-14, 57.5) * mm});
            skLineSegment(sketch, "E226.MirrorCS", {"start": v(-12, 55.9) * mm, "end": v(-12, 57.5) * mm});
            skLineSegment(sketch, "E227.MirrorCS", {"start": v(-10, 55.9) * mm, "end": v(-10, 57.5) * mm});
            skLineSegment(sketch, "E228.MirrorCS", {"start": v(-8, 55.9) * mm, "end": v(-8, 57.5) * mm});
            skLineSegment(sketch, "E229.MirrorCS", {"start": v(-6, 55.9) * mm, "end": v(-6, 57.5) * mm});
            skLineSegment(sketch, "E230.MirrorCS", {"start": v(-4, 55.9) * mm, "end": v(-4, 57.5) * mm});
            skLineSegment(sketch, "E231.MirrorCS", {"start": v(-2, 55.9) * mm, "end": v(-2, 57.5) * mm});
            skLineSegment(sketch, "E232.MirrorCS", {"start": v(0, 55.9) * mm, "end": v(0, 57.5) * mm});
            skLineSegment(sketch, "E233.MirrorCS", {"start": v(2, 55.9) * mm, "end": v(2, 57.5) * mm});
            skLineSegment(sketch, "E234.MirrorCS", {"start": v(4, 55.9) * mm, "end": v(4, 57.5) * mm});
            skLineSegment(sketch, "E235.MirrorCS", {"start": v(6, 55.9) * mm, "end": v(6, 57.5) * mm});
            skLineSegment(sketch, "E236.MirrorCS", {"start": v(8, 55.9) * mm, "end": v(8, 57.5) * mm});
            skLineSegment(sketch, "E237.MirrorCS", {"start": v(10, 55.9) * mm, "end": v(10, 57.5) * mm});
            skLineSegment(sketch, "E238.MirrorCS", {"start": v(12, 55.9) * mm, "end": v(12, 57.5) * mm});
            skLineSegment(sketch, "E239.MirrorCS", {"start": v(14, 55.9) * mm, "end": v(14, 57.5) * mm});
            skLineSegment(sketch, "E240.MirrorCS", {"start": v(16, 55.9) * mm, "end": v(16, 57.5) * mm});
            skLineSegment(sketch, "E241.MirrorCS", {"start": v(18, 55.9) * mm, "end": v(18, 57.5) * mm});
            skLineSegment(sketch, "E242.MirrorCS", {"start": v(20, 55.9) * mm, "end": v(20, 57.5) * mm});
            skLineSegment(sketch, "E243.MirrorCS", {"start": v(22, 55.9) * mm, "end": v(22, 57.5) * mm});
            skLineSegment(sketch, "E244", {"start": v(-23.8, -15.9) * mm, "end": v(-27, -15.9) * mm});
            skLineSegment(sketch, "E245", {"start": v(23.8, -15.9) * mm, "end": v(27, -15.9) * mm});
            skLineSegment(sketch, "E246", {"start": v(36.2, -15.9) * mm, "end": v(33, -15.9) * mm});
            skLineSegment(sketch, "E247", {"start": v(83.8, -15.9) * mm, "end": v(87, -15.9) * mm});
            skLineSegment(sketch, "E248", {"start": v(-36.2, -15.9) * mm, "end": v(-33, -15.9) * mm});
            skLineSegment(sketch, "E249", {"start": v(-83.8, -15.9) * mm, "end": v(-87, -15.9) * mm});
            skLineSegment(sketch, "E250", {"start": v(-23.8, 55.9) * mm, "end": v(-27, 55.9) * mm});
            skLineSegment(sketch, "E251", {"start": v(23.8, 55.9) * mm, "end": v(27, 55.9) * mm});
            skLineSegment(sketch, "E252.trimOffspring", {"start": v(-23.8, 77.5) * mm, "end": v(-23.8, 62.5) * mm});
            skLineSegment(sketch, "E253.trimOffspring", {"start": v(23.8, 77.5) * mm, "end": v(23.8, 62.5) * mm});
            skLineSegment(sketch, "E254.trimOffspring", {"start": v(27, 77.5) * mm, "end": v(27, 62.5) * mm});
            skLineSegment(sketch, "E255.trimOffspring", {"start": v(-27, 77.5) * mm, "end": v(-27, 62.5) * mm});
            skLineSegment(sketch, "E256", {"start": v(-23.8, 82.5) * mm, "end": v(-23.8, 80.9) * mm});
            skLineSegment(sketch, "E257", {"start": v(-23.8, 80.9) * mm, "end": v(23.8, 80.9) * mm});
            skLineSegment(sketch, "E258", {"start": v(23.8, 80.9) * mm, "end": v(23.8, 82.5) * mm});
            skLineSegment(sketch, "E259", {"start": v(-27, 63.5) * mm, "end": v(-23.8, 63.5) * mm});
            skLineSegment(sketch, "E260", {"start": v(-27, 65.5) * mm, "end": v(-23.8, 65.5) * mm});
            skLineSegment(sketch, "E261", {"start": v(-27, 67.5) * mm, "end": v(-23.8, 67.5) * mm});
            skLineSegment(sketch, "E262", {"start": v(27, 69.5) * mm, "end": v(23.8, 69.5) * mm});
            skLineSegment(sketch, "E263", {"start": v(-27, 71.5) * mm, "end": v(-23.8, 71.5) * mm});
            skLineSegment(sketch, "E264", {"start": v(-27, 73.5) * mm, "end": v(-23.8, 73.5) * mm});
            skLineSegment(sketch, "E265", {"start": v(-27, 75.5) * mm, "end": v(27, 75.5) * mm});
            skLineSegment(sketch, "E266", {"start": v(-27, 77.5) * mm, "end": v(27, 77.5) * mm});
            skLineSegment(sketch, "E267.trimOffspring", {"start": v(23.8, 63.5) * mm, "end": v(27, 63.5) * mm});
            skLineSegment(sketch, "E268.trimOffspring", {"start": v(23.8, 65.5) * mm, "end": v(27, 65.5) * mm});
            skLineSegment(sketch, "E269.trimOffspring", {"start": v(23.8, 67.5) * mm, "end": v(27, 67.5) * mm});
            skLineSegment(sketch, "E270.trimOffspring", {"start": v(-23.8, 69.5) * mm, "end": v(-27, 69.5) * mm});
            skLineSegment(sketch, "E271.trimOffspring", {"start": v(23.8, 71.5) * mm, "end": v(27, 71.5) * mm});
            skLineSegment(sketch, "E272.trimOffspring", {"start": v(23.8, 73.5) * mm, "end": v(27, 73.5) * mm});
            skLineSegment(sketch, "E273", {"start": v(-17.2, 62.5) * mm, "end": v(-17.2, 76.5) * mm});
            skLineSegment(sketch, "E274", {"start": v(-15.6, 62.5) * mm, "end": v(-15.6, 76.5) * mm});
            skLineSegment(sketch, "E275.1.0.0", {"start": v(-9, 62.5) * mm, "end": v(-9, 76.5) * mm});
            skLineSegment(sketch, "E275.1.0.1", {"start": v(-7.4, 62.5) * mm, "end": v(-7.4, 76.5) * mm});
            skLineSegment(sketch, "E275.2.0.0", {"start": v(-0.8, 62.5) * mm, "end": v(-0.8, 76.5) * mm});
            skLineSegment(sketch, "E275.2.0.1", {"start": v(0.8, 62.5) * mm, "end": v(0.8, 76.5) * mm});
            skLineSegment(sketch, "E275.3.0.0", {"start": v(7.4, 62.5) * mm, "end": v(7.4, 76.5) * mm});
            skLineSegment(sketch, "E275.3.0.1", {"start": v(9, 62.5) * mm, "end": v(9, 76.5) * mm});
            skLineSegment(sketch, "E275.4.0.0", {"start": v(15.6, 62.5) * mm, "end": v(15.6, 76.5) * mm});
            skLineSegment(sketch, "E275.4.0.1", {"start": v(17.2, 62.5) * mm, "end": v(17.2, 76.5) * mm});
            skLineSegment(sketch, "E275.direction1", {"start": v(-15.6, 62.5) * mm, "end": v(-9, 62.5) * mm, "construction": true});
            skLineSegment(sketch, "E276.trimOffspring", {"start": v(-9, 76.5) * mm, "end": v(-7.4, 76.5) * mm});
            skLineSegment(sketch, "E277.trimOffspring", {"start": v(-0.8, 76.5) * mm, "end": v(0.8, 76.5) * mm});
            skLineSegment(sketch, "E278.trimOffspring", {"start": v(7.4, 76.5) * mm, "end": v(9, 76.5) * mm});
            skLineSegment(sketch, "E279.trimOffspring", {"start": v(15.6, 76.5) * mm, "end": v(17.2, 76.5) * mm});
            skLineSegment(sketch, "E280", {"start": v(-15.6, 76.5) * mm, "end": v(-17.2, 76.5) * mm});
            skPoint(sketch, "E281.orphan", {"position": v(-15.6, 77.5) * mm});
            skPoint(sketch, "E282.orphan", {"position": v(-17.2, 77.5) * mm});
            skPoint(sketch, "E283.orphan", {"position": v(-9, 77.5) * mm});
            skPoint(sketch, "E284.orphan", {"position": v(-7.4, 77.5) * mm});
            skPoint(sketch, "E285.orphan", {"position": v(-0.8, 77.5) * mm});
            skPoint(sketch, "E286.orphan", {"position": v(0.8, 77.5) * mm});
            skPoint(sketch, "E287.orphan", {"position": v(7.4, 77.5) * mm});
            skPoint(sketch, "E288.orphan", {"position": v(9, 77.5) * mm});
            skPoint(sketch, "E289.orphan", {"position": v(15.6, 77.5) * mm});
            skPoint(sketch, "E290.orphan", {"position": v(17.2, 77.5) * mm});
            skLineSegment(sketch, "E291", {"start": v(42.8, 17.5) * mm, "end": v(42.8, 3.5) * mm});
            skLineSegment(sketch, "E292", {"start": v(44.4, 17.5) * mm, "end": v(44.4, 3.5) * mm});
            skLineSegment(sketch, "E293.1.0.0", {"start": v(51, 17.5) * mm, "end": v(51, 3.5) * mm});
            skLineSegment(sketch, "E293.1.0.1", {"start": v(52.6, 17.5) * mm, "end": v(52.6, 3.5) * mm});
            skLineSegment(sketch, "E293.2.0.0", {"start": v(59.2, 17.5) * mm, "end": v(59.2, 3.5) * mm});
            skLineSegment(sketch, "E293.2.0.1", {"start": v(60.8, 17.5) * mm, "end": v(60.8, 3.5) * mm});
            skLineSegment(sketch, "E293.3.0.0", {"start": v(67.4, 17.5) * mm, "end": v(67.4, 3.5) * mm});
            skLineSegment(sketch, "E293.3.0.1", {"start": v(69, 17.5) * mm, "end": v(69, 3.5) * mm});
            skLineSegment(sketch, "E293.4.0.0", {"start": v(75.6, 17.5) * mm, "end": v(75.6, 3.5) * mm});
            skLineSegment(sketch, "E293.4.0.1", {"start": v(77.2, 17.5) * mm, "end": v(77.2, 3.5) * mm});
            skLineSegment(sketch, "E293.direction1", {"start": v(42.8, 3.5) * mm, "end": v(51, 3.5) * mm, "construction": true});
            skLineSegment(sketch, "E294", {"start": v(42.8, 3.5) * mm, "end": v(44.4, 3.5) * mm});
            skLineSegment(sketch, "E295", {"start": v(51, 3.5) * mm, "end": v(52.6, 3.5) * mm});
            skLineSegment(sketch, "E296", {"start": v(59.2, 3.5) * mm, "end": v(60.8, 3.5) * mm});
            skLineSegment(sketch, "E297", {"start": v(67.4, 3.5) * mm, "end": v(69, 3.5) * mm});
            skLineSegment(sketch, "E298", {"start": v(75.6, 3.5) * mm, "end": v(77.2, 3.5) * mm});
            skLineSegment(sketch, "E299", {"start": v(37.2, 2.5) * mm, "end": v(37.2, 0.9) * mm});
            skLineSegment(sketch, "E300", {"start": v(37.2, 2.5) * mm, "end": v(82.8, 2.5) * mm});
            skLineSegment(sketch, "E301", {"start": v(82.8, 0.9) * mm, "end": v(82.8, 2.5) * mm});
            skLineSegment(sketch, "E302", {"start": v(37.2, 0.9) * mm, "end": v(82.8, 0.9) * mm});
            skLineSegment(sketch, "E303", {"start": v(37.2, -7.8) * mm, "end": v(37.2, -6.2) * mm});
            skLineSegment(sketch, "E304", {"start": v(37.2, -6.2) * mm, "end": v(83.8, -6.2) * mm});
            skLineSegment(sketch, "E305", {"start": v(37.2, -7.8) * mm, "end": v(83.8, -7.8) * mm});
            skLineSegment(sketch, "E306.trimOffspring", {"start": v(83.8, -7.8) * mm, "end": v(83.8, -17.5) * mm});
            skLineSegment(sketch, "E307", {"start": v(82.8, -6.2) * mm, "end": v(82.8, -7.8) * mm});
            skLineSegment(sketch, "E308", {"start": v(83.8, -6.2) * mm, "end": v(83.8, -7.8) * mm});
            skLineSegment(sketch, "E309.trimOffspring", {"start": v(42.8, 17.5) * mm, "end": v(33, 17.5) * mm});
            skLineSegment(sketch, "E310.trimOffspring", {"start": v(51, 17.5) * mm, "end": v(44.4, 17.5) * mm});
            skLineSegment(sketch, "E311.trimOffspring", {"start": v(69, 17.5) * mm, "end": v(75.6, 17.5) * mm});
            skLineSegment(sketch, "E312.trimOffspring", {"start": v(77.2, 17.5) * mm, "end": v(87, 17.5) * mm});
            skLineSegment(sketch, "E313.trimOffspring", {"start": v(-7.4, 62.5) * mm, "end": v(-0.8, 62.5) * mm});
            skLineSegment(sketch, "E314.trimOffspring", {"start": v(-15.6, 62.5) * mm, "end": v(-9, 62.5) * mm});
            skLineSegment(sketch, "E315.trimOffspring", {"start": v(7.4, 62.5) * mm, "end": v(0.8, 62.5) * mm});
            skLineSegment(sketch, "E316.trimOffspring", {"start": v(15.6, 62.5) * mm, "end": v(9, 62.5) * mm});
            skLineSegment(sketch, "E317", {"start": v(-17.2, 22.5) * mm, "end": v(-17.2, 36.5) * mm});
            skLineSegment(sketch, "E318", {"start": v(-17.2, 36.5) * mm, "end": v(-15.6, 36.5) * mm});
            skLineSegment(sketch, "E319", {"start": v(-15.6, 36.5) * mm, "end": v(-15.6, 22.5) * mm});
            skLineSegment(sketch, "E320.1.0.0", {"start": v(-7.4, 36.5) * mm, "end": v(-7.4, 22.5) * mm});
            skLineSegment(sketch, "E320.1.0.1", {"start": v(-9, 22.5) * mm, "end": v(-9, 36.5) * mm});
            skLineSegment(sketch, "E320.1.0.2", {"start": v(-9, 36.5) * mm, "end": v(-7.4, 36.5) * mm});
            skLineSegment(sketch, "E320.2.0.0", {"start": v(0.8, 36.5) * mm, "end": v(0.8, 22.5) * mm});
            skLineSegment(sketch, "E320.2.0.1", {"start": v(-0.8, 22.5) * mm, "end": v(-0.8, 36.5) * mm});
            skLineSegment(sketch, "E320.2.0.2", {"start": v(-0.8, 36.5) * mm, "end": v(0.8, 36.5) * mm});
            skLineSegment(sketch, "E320.3.0.0", {"start": v(9, 36.5) * mm, "end": v(9, 22.5) * mm});
            skLineSegment(sketch, "E320.3.0.1", {"start": v(7.4, 22.5) * mm, "end": v(7.4, 36.5) * mm});
            skLineSegment(sketch, "E320.3.0.2", {"start": v(7.4, 36.5) * mm, "end": v(9, 36.5) * mm});
            skLineSegment(sketch, "E320.4.0.0", {"start": v(17.2, 36.5) * mm, "end": v(17.2, 22.5) * mm});
            skLineSegment(sketch, "E320.4.0.1", {"start": v(15.6, 22.5) * mm, "end": v(15.6, 36.5) * mm});
            skLineSegment(sketch, "E320.4.0.2", {"start": v(15.6, 36.5) * mm, "end": v(17.2, 36.5) * mm});
            skLineSegment(sketch, "E320.direction1", {"start": v(-15.6, 22.5) * mm, "end": v(-9, 22.5) * mm, "construction": true});
            skLineSegment(sketch, "E321", {"start": v(-22.8, 37.5) * mm, "end": v(-22.8, 39.1) * mm});
            skLineSegment(sketch, "E322", {"start": v(-22.8, 39.1) * mm, "end": v(22.8, 39.1) * mm});
            skLineSegment(sketch, "E323", {"start": v(22.8, 39.1) * mm, "end": v(22.8, 37.5) * mm});
            skLineSegment(sketch, "E324", {"start": v(22.8, 37.5) * mm, "end": v(-22.8, 37.5) * mm});
            skLineSegment(sketch, "E325.trimOffspring", {"start": v(-17.2, 22.5) * mm, "end": v(-27, 22.5) * mm});
            skLineSegment(sketch, "E326.trimOffspring", {"start": v(-9, 22.5) * mm, "end": v(-15.6, 22.5) * mm});
            skPoint(sketch, "E327.orphan", {"position": v(0, 22.5) * mm});
            skLineSegment(sketch, "E328.trimOffspring", {"start": v(9, 22.5) * mm, "end": v(15.6, 22.5) * mm});
            skLineSegment(sketch, "E329.trimOffspring", {"start": v(17.2, 22.5) * mm, "end": v(27, 22.5) * mm});
            skLineSegment(sketch, "E330.bottom", {"start": v(22.8, -28.12) * mm, "end": v(-22.8, -28.12) * mm});
            skLineSegment(sketch, "E330.top", {"start": v(22.8, -78.92) * mm, "end": v(-22.8, -78.92) * mm});
            skLineSegment(sketch, "E330.left", {"start": v(25.4, -30.72) * mm, "end": v(25.4, -76.32) * mm});
            skLineSegment(sketch, "E330.right", {"start": v(-25.4, -30.72) * mm, "end": v(-25.4, -76.32) * mm});
            skPoint(sketch, "E330.middle", {"position": v(0, -53.52) * mm});
            skLineSegment(sketch, "E331.0", {"start": v(23.8, -29.72) * mm, "end": v(22.8, -29.72) * mm});
            skLineSegment(sketch, "E331.1", {"start": v(23.8, -29.72) * mm, "end": v(23.8, -30.72) * mm});
            skLineSegment(sketch, "E331.2", {"start": v(23.8, -77.32) * mm, "end": v(22.8, -77.32) * mm});
            skLineSegment(sketch, "E331.3", {"start": v(-23.8, -29.72) * mm, "end": v(-23.8, -30.72) * mm});
            skLineSegment(sketch, "E332", {"start": v(22.8, -28.12) * mm, "end": v(22.8, -29.72) * mm});
            skLineSegment(sketch, "E333", {"start": v(23.8, -30.72) * mm, "end": v(25.4, -30.72) * mm});
            skLineSegment(sketch, "E334", {"start": v(0, -20) * mm, "end": v(0, -88.2) * mm, "construction": true});
            skLineSegment(sketch, "E335", {"start": v(-38.13, -53.52) * mm, "end": v(32.43, -53.52) * mm, "construction": true});
            skPoint(sketch, "E335.startSnap0", {"position": v(-25.4, -53.52) * mm});
            skPoint(sketch, "E335.endSnap0", {"position": v(25.4, -53.52) * mm});
            skLineSegment(sketch, "E336.MirrorCS", {"start": v(22.8, -78.92) * mm, "end": v(22.8, -77.32) * mm});
            skLineSegment(sketch, "E337.MirrorCS", {"start": v(23.8, -76.32) * mm, "end": v(25.4, -76.32) * mm});
            skLineSegment(sketch, "E338.MirrorCS", {"start": v(-23.8, -30.72) * mm, "end": v(-25.4, -30.72) * mm});
            skLineSegment(sketch, "E339.MirrorCS", {"start": v(-23.8, -76.32) * mm, "end": v(-25.4, -76.32) * mm});
            skLineSegment(sketch, "E340.MirrorCS", {"start": v(-22.8, -78.92) * mm, "end": v(-22.8, -77.32) * mm});
            skLineSegment(sketch, "E341.MirrorCS", {"start": v(-22.8, -28.12) * mm, "end": v(-22.8, -29.72) * mm});
            skPoint(sketch, "E342.orphan", {"position": v(-25.4, -28.12) * mm});
            skPoint(sketch, "E343.orphan", {"position": v(25.4, -28.12) * mm});
            skPoint(sketch, "E344.orphan", {"position": v(-25.4, -78.92) * mm});
            skPoint(sketch, "E345.orphan", {"position": v(25.4, -78.92) * mm});
            skPoint(sketch, "E346.orphan", {"position": v(-22.8, -30.72) * mm});
            skPoint(sketch, "E347.orphan", {"position": v(22.8, -30.72) * mm});
            skPoint(sketch, "E348.orphan", {"position": v(22.8, -76.32) * mm});
            skPoint(sketch, "E349.orphan", {"position": v(-22.8, -76.32) * mm});
            skLineSegment(sketch, "E350.trimOffspring", {"start": v(-23.8, -76.32) * mm, "end": v(-23.8, -77.32) * mm});
            skLineSegment(sketch, "E351.trimOffspring", {"start": v(-22.8, -29.72) * mm, "end": v(-23.8, -29.72) * mm});
            skLineSegment(sketch, "E352.trimOffspring", {"start": v(23.8, -76.32) * mm, "end": v(23.8, -77.32) * mm});
            skLineSegment(sketch, "E353.trimOffspring", {"start": v(-22.8, -77.32) * mm, "end": v(-23.8, -77.32) * mm});
            skLineSegment(sketch, "E354.bottom", {"start": v(82.73, -26.52) * mm, "end": v(38.73, -26.52) * mm});
            skLineSegment(sketch, "E354.left", {"start": v(87.73, -31.52) * mm, "end": v(87.73, -75.52) * mm});
            skPoint(sketch, "E354.middle", {"position": v(60.73, -53.52) * mm});
            skLineSegment(sketch, "E355", {"start": v(36.93, -29.72) * mm, "end": v(84.53, -29.72) * mm});
            skLineSegment(sketch, "E356", {"start": v(84.53, -29.72) * mm, "end": v(84.53, -77.32) * mm});
            skLineSegment(sketch, "E357", {"start": v(84.53, -77.32) * mm, "end": v(36.93, -77.32) * mm});
            skLineSegment(sketch, "E358", {"start": v(36.93, -77.32) * mm, "end": v(36.93, -29.72) * mm});
            skLineSegment(sketch, "E359", {"start": v(38.73, -26.52) * mm, "end": v(38.73, -29.72) * mm});
            skLineSegment(sketch, "E360", {"start": v(33.73, -31.52) * mm, "end": v(36.93, -31.52) * mm});
            skLineSegment(sketch, "E361", {"start": v(32.43, -53.52) * mm, "end": v(93.03, -53.52) * mm, "construction": true});
            skPoint(sketch, "E361.endSnap0", {"position": v(87.73, -53.52) * mm});
            skLineSegment(sketch, "E362", {"start": v(60.73, -86.6) * mm, "end": v(60.73, -29.72) * mm, "construction": true});
            skPoint(sketch, "E362.startSnap0", {"position": v(60.73, -80.52) * mm});
            skPoint(sketch, "E362.endSnap0", {"position": v(60.73, -26.52) * mm});
            skLineSegment(sketch, "E363.MirrorCS", {"start": v(82.73, -26.52) * mm, "end": v(82.73, -29.72) * mm});
            skLineSegment(sketch, "E364.MirrorCS", {"start": v(87.73, -31.52) * mm, "end": v(84.53, -31.52) * mm});
            skLineSegment(sketch, "E365.MirrorCS", {"start": v(87.73, -75.52) * mm, "end": v(84.53, -75.52) * mm});
            skLineSegment(sketch, "E366.MirrorCS", {"start": v(33.73, -75.52) * mm, "end": v(36.93, -75.52) * mm});
            skLineSegment(sketch, "E367", {"start": v(40.73, -26.52) * mm, "end": v(40.73, -29.72) * mm});
            skLineSegment(sketch, "E368", {"start": v(33.73, -33.52) * mm, "end": v(36.93, -33.52) * mm});
            skLineSegment(sketch, "E369.1.0.0", {"start": v(42.73, -26.52) * mm, "end": v(42.73, -29.72) * mm});
            skLineSegment(sketch, "E369.1.0.1", {"start": v(44.73, -26.52) * mm, "end": v(44.73, -29.72) * mm});
            skLineSegment(sketch, "E369.2.0.0", {"start": v(46.73, -26.52) * mm, "end": v(46.73, -29.72) * mm});
            skLineSegment(sketch, "E369.2.0.1", {"start": v(48.73, -26.52) * mm, "end": v(48.73, -29.72) * mm});
            skLineSegment(sketch, "E369.3.0.0", {"start": v(50.73, -26.52) * mm, "end": v(50.73, -29.72) * mm});
            skLineSegment(sketch, "E369.3.0.1", {"start": v(52.73, -26.52) * mm, "end": v(52.73, -29.72) * mm});
            skLineSegment(sketch, "E369.4.0.0", {"start": v(54.73, -26.52) * mm, "end": v(54.73, -29.72) * mm});
            skLineSegment(sketch, "E369.4.0.1", {"start": v(56.73, -26.52) * mm, "end": v(56.73, -29.72) * mm});
            skLineSegment(sketch, "E369.5.0.0", {"start": v(58.73, -26.52) * mm, "end": v(58.73, -29.72) * mm});
            skLineSegment(sketch, "E369.5.0.1", {"start": v(60.73, -26.52) * mm, "end": v(60.73, -29.72) * mm});
            skLineSegment(sketch, "E369.6.0.0", {"start": v(62.73, -26.52) * mm, "end": v(62.73, -29.72) * mm});
            skLineSegment(sketch, "E369.6.0.1", {"start": v(64.73, -26.52) * mm, "end": v(64.73, -29.72) * mm});
            skLineSegment(sketch, "E369.7.0.0", {"start": v(66.73, -26.52) * mm, "end": v(66.73, -29.72) * mm});
            skLineSegment(sketch, "E369.7.0.1", {"start": v(68.73, -26.52) * mm, "end": v(68.73, -29.72) * mm});
            skLineSegment(sketch, "E369.8.0.0", {"start": v(70.73, -26.52) * mm, "end": v(70.73, -29.72) * mm});
            skLineSegment(sketch, "E369.8.0.1", {"start": v(72.73, -26.52) * mm, "end": v(72.73, -29.72) * mm});
            skLineSegment(sketch, "E369.9.0.0", {"start": v(74.73, -26.52) * mm, "end": v(74.73, -29.72) * mm});
            skLineSegment(sketch, "E369.9.0.1", {"start": v(76.73, -26.52) * mm, "end": v(76.73, -29.72) * mm});
            skLineSegment(sketch, "E369.direction1", {"start": v(38.73, -29.72) * mm, "end": v(42.73, -29.72) * mm, "construction": true});
            skLineSegment(sketch, "E370.0.10.0", {"start": v(78.73, -26.52) * mm, "end": v(78.73, -29.72) * mm});
            skLineSegment(sketch, "E370.3.10.0", {"start": v(80.73, -26.52) * mm, "end": v(80.73, -29.72) * mm});
            skLineSegment(sketch, "E371.1.0.0", {"start": v(33.73, -35.52) * mm, "end": v(36.93, -35.52) * mm});
            skLineSegment(sketch, "E371.1.0.1", {"start": v(33.73, -37.52) * mm, "end": v(36.93, -37.52) * mm});
            skLineSegment(sketch, "E371.2.0.0", {"start": v(33.73, -39.52) * mm, "end": v(36.93, -39.52) * mm});
            skLineSegment(sketch, "E371.2.0.1", {"start": v(33.73, -41.52) * mm, "end": v(36.93, -41.52) * mm});
            skLineSegment(sketch, "E371.3.0.0", {"start": v(33.73, -43.52) * mm, "end": v(36.93, -43.52) * mm});
            skLineSegment(sketch, "E371.3.0.1", {"start": v(33.73, -45.52) * mm, "end": v(36.93, -45.52) * mm});
            skLineSegment(sketch, "E371.4.0.0", {"start": v(33.73, -47.52) * mm, "end": v(36.93, -47.52) * mm});
            skLineSegment(sketch, "E371.4.0.1", {"start": v(33.73, -49.52) * mm, "end": v(36.93, -49.52) * mm});
            skLineSegment(sketch, "E371.5.0.0", {"start": v(33.73, -51.52) * mm, "end": v(36.93, -51.52) * mm});
            skLineSegment(sketch, "E371.5.0.1", {"start": v(33.73, -53.52) * mm, "end": v(36.93, -53.52) * mm});
            skLineSegment(sketch, "E371.6.0.0", {"start": v(33.73, -55.52) * mm, "end": v(36.93, -55.52) * mm});
            skLineSegment(sketch, "E371.6.0.1", {"start": v(33.73, -57.52) * mm, "end": v(36.93, -57.52) * mm});
            skLineSegment(sketch, "E371.7.0.0", {"start": v(33.73, -59.52) * mm, "end": v(36.93, -59.52) * mm});
            skLineSegment(sketch, "E371.7.0.1", {"start": v(33.73, -61.52) * mm, "end": v(36.93, -61.52) * mm});
            skLineSegment(sketch, "E371.8.0.0", {"start": v(33.73, -63.52) * mm, "end": v(36.93, -63.52) * mm});
            skLineSegment(sketch, "E371.8.0.1", {"start": v(33.73, -65.52) * mm, "end": v(36.93, -65.52) * mm});
            skLineSegment(sketch, "E371.9.0.0", {"start": v(33.73, -67.52) * mm, "end": v(36.93, -67.52) * mm});
            skLineSegment(sketch, "E371.9.0.1", {"start": v(33.73, -69.52) * mm, "end": v(36.93, -69.52) * mm});
            skLineSegment(sketch, "E371.direction1", {"start": v(33.73, -33.52) * mm, "end": v(33.73, -37.52) * mm, "construction": true});
            skLineSegment(sketch, "E372.0.10.0", {"start": v(33.73, -71.52) * mm, "end": v(36.93, -71.52) * mm});
            skLineSegment(sketch, "E372.3.10.0", {"start": v(33.73, -73.52) * mm, "end": v(36.93, -73.52) * mm});
            skLineSegment(sketch, "E373.trimOffspring", {"start": v(60.73, -26.52) * mm, "end": v(60.73, -23.23) * mm, "construction": true});
            skLineSegment(sketch, "E374.MirrorCS", {"start": v(60.73, -80.52) * mm, "end": v(60.73, -77.32) * mm});
            skLineSegment(sketch, "E375.MirrorCS", {"start": v(87.73, -33.52) * mm, "end": v(84.53, -33.52) * mm});
            skLineSegment(sketch, "E376.MirrorCS", {"start": v(87.73, -35.52) * mm, "end": v(84.53, -35.52) * mm});
            skLineSegment(sketch, "E377.MirrorCS", {"start": v(87.73, -37.52) * mm, "end": v(84.53, -37.52) * mm});
            skLineSegment(sketch, "E378.MirrorCS", {"start": v(87.73, -39.52) * mm, "end": v(84.53, -39.52) * mm});
            skLineSegment(sketch, "E379.MirrorCS", {"start": v(87.73, -41.52) * mm, "end": v(84.53, -41.52) * mm});
            skLineSegment(sketch, "E380.MirrorCS", {"start": v(87.73, -43.52) * mm, "end": v(84.53, -43.52) * mm});
            skLineSegment(sketch, "E381.MirrorCS", {"start": v(87.73, -45.52) * mm, "end": v(84.53, -45.52) * mm});
            skLineSegment(sketch, "E382.MirrorCS", {"start": v(87.73, -47.52) * mm, "end": v(84.53, -47.52) * mm});
            skLineSegment(sketch, "E383.MirrorCS", {"start": v(87.73, -49.52) * mm, "end": v(84.53, -49.52) * mm});
            skLineSegment(sketch, "E384.MirrorCS", {"start": v(87.73, -51.52) * mm, "end": v(84.53, -51.52) * mm});
            skLineSegment(sketch, "E385.MirrorCS", {"start": v(87.73, -55.52) * mm, "end": v(84.53, -55.52) * mm});
            skLineSegment(sketch, "E386.MirrorCS", {"start": v(87.73, -57.52) * mm, "end": v(84.53, -57.52) * mm});
            skLineSegment(sketch, "E387.MirrorCS", {"start": v(87.73, -59.52) * mm, "end": v(84.53, -59.52) * mm});
            skLineSegment(sketch, "E388.MirrorCS", {"start": v(87.73, -61.52) * mm, "end": v(84.53, -61.52) * mm});
            skLineSegment(sketch, "E389.MirrorCS", {"start": v(87.73, -63.52) * mm, "end": v(84.53, -63.52) * mm});
            skLineSegment(sketch, "E390.MirrorCS", {"start": v(87.73, -65.52) * mm, "end": v(84.53, -65.52) * mm});
            skLineSegment(sketch, "E391.MirrorCS", {"start": v(87.73, -67.52) * mm, "end": v(84.53, -67.52) * mm});
            skLineSegment(sketch, "E392.MirrorCS", {"start": v(87.73, -69.52) * mm, "end": v(84.53, -69.52) * mm});
            skLineSegment(sketch, "E393.MirrorCS", {"start": v(87.73, -73.52) * mm, "end": v(84.53, -73.52) * mm});
            skLineSegment(sketch, "E394.MirrorCS", {"start": v(87.73, -71.52) * mm, "end": v(84.53, -71.52) * mm});
            skLineSegment(sketch, "E395.trimOffspring", {"start": v(33.73, -31.52) * mm, "end": v(33.73, -75.52) * mm});
            skPoint(sketch, "E354.right.start.orphan", {"position": v(33.73, -26.52) * mm});
            skPoint(sketch, "E396.orphan", {"position": v(87.73, -26.52) * mm});
            skPoint(sketch, "E397.orphan", {"position": v(87.73, -80.52) * mm});
            skPoint(sketch, "E398.orphan", {"position": v(33.73, -80.52) * mm});
            skPoint(sketch, "E399.startSnap0", {"position": v(-22.8, 38.3) * mm});
            skLineSegment(sketch, "E400", {"start": v(-23.8, 41.5) * mm, "end": v(-27, 41.5) * mm});
            skLineSegment(sketch, "E401.MirrorCS", {"start": v(23.8, 41.5) * mm, "end": v(27, 41.5) * mm});
            skLineSegment(sketch, "E402", {"start": v(87.73, -53.52) * mm, "end": v(84.53, -53.52) * mm});
            skLineSegment(sketch, "E403", {"start": v(36.93, -77.32) * mm, "end": v(36.93, -80.52) * mm});
            skLineSegment(sketch, "E404", {"start": v(36.93, -80.52) * mm, "end": v(84.53, -80.52) * mm});
            skLineSegment(sketch, "E405", {"start": v(84.53, -80.52) * mm, "end": v(84.53, -77.32) * mm});
            skSolve(sketch);
        }
        {
            var Q0;
            {var subQ14=sQuery(id+"F0.wireOp",EDGE,"E256");Q0=makeQuery(id+"F0.imprint","IMPRINT",FACE,{"disambiguationData":[TD([[makeQuery(id+"F0.imprint","IMPRINT",EDGE,{"derivedFrom":subQ14}),1.0]])]});}
            var Q1;
            {var subQ0=sQuery(id+"F0.wireOp",EDGE,"E107.MirrorCS");Q1=makeQuery(id+"F0.imprint","IMPRINT",FACE,{"disambiguationData":[TD([[makeQuery(id+"F0.imprint","IMPRINT",EDGE,{"derivedFrom":subQ0}),1.0]])]});}
            var Q2;
            {var subQ0=sQuery(id+"F0.wireOp",EDGE,"E117.MirrorCS");Q2=makeQuery(id+"F0.imprint","IMPRINT",FACE,{"disambiguationData":[TD([[makeQuery(id+"F0.imprint","IMPRINT",EDGE,{"derivedFrom":subQ0}),-1.0]])]});}
            var Q3;
            {var subQ0=sQuery(id+"F0.wireOp",EDGE,"E109.MirrorCS");Q3=makeQuery(id+"F0.imprint","IMPRINT",FACE,{"disambiguationData":[TD([[makeQuery(id+"F0.imprint","IMPRINT",EDGE,{"derivedFrom":subQ0}),1.0]])]});}
            var Q4;
            {var subQ0=sQuery(id+"F0.wireOp",EDGE,"E119.MirrorCS");Q4=makeQuery(id+"F0.imprint","IMPRINT",FACE,{"disambiguationData":[TD([[makeQuery(id+"F0.imprint","IMPRINT",EDGE,{"derivedFrom":subQ0}),-1.0]])]});}
            var Q5;
            {var subQ0=sQuery(id+"F0.wireOp",EDGE,"E111.MirrorCS");Q5=makeQuery(id+"F0.imprint","IMPRINT",FACE,{"disambiguationData":[TD([[makeQuery(id+"F0.imprint","IMPRINT",EDGE,{"derivedFrom":subQ0}),1.0]])]});}
            var Q6;
            {var subQ0=sQuery(id+"F0.wireOp",EDGE,"E113.MirrorCS");Q6=makeQuery(id+"F0.imprint","IMPRINT",FACE,{"disambiguationData":[TD([[makeQuery(id+"F0.imprint","IMPRINT",EDGE,{"derivedFrom":subQ0}),1.0]])]});}
            var Q7;
            {var subQ0=sQuery(id+"F0.wireOp",EDGE,"E115.MirrorCS");Q7=makeQuery(id+"F0.imprint","IMPRINT",FACE,{"disambiguationData":[TD([[makeQuery(id+"F0.imprint","IMPRINT",EDGE,{"derivedFrom":subQ0}),1.0]])]});}
            var Q8;
            {var subQ0=sQuery(id+"F0.wireOp",EDGE,"E121.MirrorCS");Q8=makeQuery(id+"F0.imprint","IMPRINT",FACE,{"disambiguationData":[TD([[makeQuery(id+"F0.imprint","IMPRINT",EDGE,{"derivedFrom":subQ0}),-1.0]])]});}
            var Q9;
            {var subQ16=sQuery(id+"F0.wireOp",EDGE,"E276.trimOffspring");Q9=makeQuery(id+"F0.imprint","IMPRINT",FACE,{"disambiguationData":[TD([[makeQuery(id+"F0.imprint","IMPRINT",EDGE,{"derivedFrom":subQ16}),1.0]])]});}
            var Q10;
            {var subQ5=sQuery(id+"F0.wireOp",EDGE,"E315.trimOffspring");Q10=makeQuery(id+"F0.imprint","IMPRINT",FACE,{"disambiguationData":[TD([[makeQuery(id+"F0.imprint","IMPRINT",EDGE,{"derivedFrom":subQ5}),-1.0]])]});}
            var Q11;
            {var subQ5=sQuery(id+"F0.wireOp",EDGE,"E313.trimOffspring");Q11=makeQuery(id+"F0.imprint","IMPRINT",FACE,{"disambiguationData":[TD([[makeQuery(id+"F0.imprint","IMPRINT",EDGE,{"derivedFrom":subQ5}),1.0]])]});}
            var Q12;
            {var subQ5=sQuery(id+"F0.wireOp",EDGE,"E314.trimOffspring");Q12=makeQuery(id+"F0.imprint","IMPRINT",FACE,{"disambiguationData":[TD([[makeQuery(id+"F0.imprint","IMPRINT",EDGE,{"derivedFrom":subQ5}),1.0]])]});}
            var Q13;
            {var subQ6=sQuery(id+"F0.wireOp",EDGE,"E273");var subQ7=sQuery(id+"F0.wireOp",EDGE,"E104.MirrorCS");var subQ8=makeQuery(id+"F0.imprint","INTERSECT",VERTEX,{"derivedFrom":[subQ7,subQ6]});Q13=makeQuery(id+"F0.imprint","IMPRINT",FACE,{"disambiguationData":[TD([[makeQuery(id+"F0.imprint","IMPRINT",EDGE,{"disambiguationData":[TD([[subQ8,1.0]])],"derivedFrom":subQ7}),1.0]])]});}
            var Q14;
            {var subQ3=sQuery(id+"F0.wireOp",EDGE,"E275.4.0.1");var subQ4=sQuery(id+"F0.wireOp",EDGE,"E103.MirrorCS");var subQ5=makeQuery(id+"F0.imprint","INTERSECT",VERTEX,{"derivedFrom":[subQ4,subQ3]});Q14=makeQuery(id+"F0.imprint","IMPRINT",FACE,{"disambiguationData":[TD([[makeQuery(id+"F0.imprint","IMPRINT",EDGE,{"disambiguationData":[TD([[subQ5,1.0]])],"derivedFrom":subQ4}),-1.0]])]});}
            var Q15;
            {var subQ5=sQuery(id+"F0.wireOp",EDGE,"E316.trimOffspring");Q15=makeQuery(id+"F0.imprint","IMPRINT",FACE,{"disambiguationData":[TD([[makeQuery(id+"F0.imprint","IMPRINT",EDGE,{"derivedFrom":subQ5}),-1.0]])]});}
            var Q16;
            {var subQ0=sQuery(id+"F0.wireOp",EDGE,"E266");var subQ1=sQuery(id+"F0.wireOp",EDGE,"E252.trimOffspring");var subQ2=makeQuery(id+"F0.imprint","INTERSECT",VERTEX,{"derivedFrom":[subQ1,subQ0]});Q16=makeQuery(id+"F0.imprint","IMPRINT",FACE,{"disambiguationData":[TD([[makeQuery(id+"F0.imprint","IMPRINT",EDGE,{"disambiguationData":[TD([[subQ2,-1.0]])],"derivedFrom":subQ1}),-1.0]])]});}
            var Q17;
            {var subQ0=sQuery(id+"F0.wireOp",EDGE,"E263");Q17=makeQuery(id+"F0.imprint","IMPRINT",FACE,{"disambiguationData":[TD([[makeQuery(id+"F0.imprint","IMPRINT",EDGE,{"derivedFrom":subQ0}),1.0]])]});}
            var Q18;
            {var subQ0=sQuery(id+"F0.wireOp",EDGE,"E261");Q18=makeQuery(id+"F0.imprint","IMPRINT",FACE,{"disambiguationData":[TD([[makeQuery(id+"F0.imprint","IMPRINT",EDGE,{"derivedFrom":subQ0}),1.0]])]});}
            var Q19;
            {var subQ0=sQuery(id+"F0.wireOp",EDGE,"E259");Q19=makeQuery(id+"F0.imprint","IMPRINT",FACE,{"disambiguationData":[TD([[makeQuery(id+"F0.imprint","IMPRINT",EDGE,{"derivedFrom":subQ0}),1.0]])]});}
            var Q20;
            {var subQ0=sQuery(id+"F0.wireOp",EDGE,"E267.trimOffspring");Q20=makeQuery(id+"F0.imprint","IMPRINT",FACE,{"disambiguationData":[TD([[makeQuery(id+"F0.imprint","IMPRINT",EDGE,{"derivedFrom":subQ0}),1.0]])]});}
            var Q21;
            {var subQ0=sQuery(id+"F0.wireOp",EDGE,"E262");Q21=makeQuery(id+"F0.imprint","IMPRINT",FACE,{"disambiguationData":[TD([[makeQuery(id+"F0.imprint","IMPRINT",EDGE,{"derivedFrom":subQ0}),1.0]])]});}
            var Q22;
            {var subQ0=sQuery(id+"F0.wireOp",EDGE,"E271.trimOffspring");Q22=makeQuery(id+"F0.imprint","IMPRINT",FACE,{"disambiguationData":[TD([[makeQuery(id+"F0.imprint","IMPRINT",EDGE,{"derivedFrom":subQ0}),1.0]])]});}
            var Q23;
            {var subQ0=sQuery(id+"F0.wireOp",EDGE,"E266");var subQ1=sQuery(id+"F0.wireOp",EDGE,"E253.trimOffspring");var subQ2=makeQuery(id+"F0.imprint","INTERSECT",VERTEX,{"derivedFrom":[subQ1,subQ0]});Q23=makeQuery(id+"F0.imprint","IMPRINT",FACE,{"disambiguationData":[TD([[makeQuery(id+"F0.imprint","IMPRINT",EDGE,{"disambiguationData":[TD([[subQ2,-1.0]])],"derivedFrom":subQ1}),1.0]])]});}
            var Q24;
            {var subQ0=sQuery(id+"F0.wireOp",EDGE,"E33.MirrorCS");Q24=makeQuery(id+"F0.imprint","IMPRINT",FACE,{"disambiguationData":[TD([[makeQuery(id+"F0.imprint","IMPRINT",EDGE,{"derivedFrom":subQ0}),1.0]])]});}
            var Q25;
            {var subQ0=sQuery(id+"F0.wireOp",EDGE,"E35.MirrorCS");Q25=makeQuery(id+"F0.imprint","IMPRINT",FACE,{"disambiguationData":[TD([[makeQuery(id+"F0.imprint","IMPRINT",EDGE,{"derivedFrom":subQ0}),1.0]])]});}
            var Q26;
            {var subQ0=sQuery(id+"F0.wireOp",EDGE,"E37.MirrorCS");Q26=makeQuery(id+"F0.imprint","IMPRINT",FACE,{"disambiguationData":[TD([[makeQuery(id+"F0.imprint","IMPRINT",EDGE,{"derivedFrom":subQ0}),1.0]])]});}
            var Q27;
            {var subQ0=sQuery(id+"F0.wireOp",EDGE,"E39.MirrorCS");Q27=makeQuery(id+"F0.imprint","IMPRINT",FACE,{"disambiguationData":[TD([[makeQuery(id+"F0.imprint","IMPRINT",EDGE,{"derivedFrom":subQ0}),1.0]])]});}
            var Q28;
            {var subQ0=sQuery(id+"F0.wireOp",EDGE,"E42.MirrorCS");Q28=makeQuery(id+"F0.imprint","IMPRINT",FACE,{"disambiguationData":[TD([[makeQuery(id+"F0.imprint","IMPRINT",EDGE,{"derivedFrom":subQ0}),1.0]])]});}
            var Q29;
            {var subQ0=sQuery(id+"F0.wireOp",EDGE,"E44.MirrorCS");Q29=makeQuery(id+"F0.imprint","IMPRINT",FACE,{"disambiguationData":[TD([[makeQuery(id+"F0.imprint","IMPRINT",EDGE,{"derivedFrom":subQ0}),1.0]])]});}
            var Q30;
            {var subQ5=sQuery(id+"F0.wireOp",EDGE,"E251");Q30=makeQuery(id+"F0.imprint","IMPRINT",FACE,{"disambiguationData":[TD([[makeQuery(id+"F0.imprint","IMPRINT",EDGE,{"derivedFrom":subQ5}),1.0]])]});}
            var Q31;
            {var subQ5=sQuery(id+"F0.wireOp",EDGE,"E250");Q31=makeQuery(id+"F0.imprint","IMPRINT",FACE,{"disambiguationData":[TD([[makeQuery(id+"F0.imprint","IMPRINT",EDGE,{"derivedFrom":subQ5}),-1.0]])]});}
            var Q32;
            {var subQ0=sQuery(id+"F0.wireOp",EDGE,"E50.MirrorCS");Q32=makeQuery(id+"F0.imprint","IMPRINT",FACE,{"disambiguationData":[TD([[makeQuery(id+"F0.imprint","IMPRINT",EDGE,{"derivedFrom":subQ0}),1.0]])]});}
            var Q33;
            {var subQ0=sQuery(id+"F0.wireOp",EDGE,"E54.MirrorCS");Q33=makeQuery(id+"F0.imprint","IMPRINT",FACE,{"disambiguationData":[TD([[makeQuery(id+"F0.imprint","IMPRINT",EDGE,{"derivedFrom":subQ0}),1.0]])]});}
            var Q34;
            {var subQ0=sQuery(id+"F0.wireOp",EDGE,"E63.MirrorCS");Q34=makeQuery(id+"F0.imprint","IMPRINT",FACE,{"disambiguationData":[TD([[makeQuery(id+"F0.imprint","IMPRINT",EDGE,{"derivedFrom":subQ0}),1.0]])]});}
            var Q35;
            {var subQ0=sQuery(id+"F0.wireOp",EDGE,"E61.MirrorCS");Q35=makeQuery(id+"F0.imprint","IMPRINT",FACE,{"disambiguationData":[TD([[makeQuery(id+"F0.imprint","IMPRINT",EDGE,{"derivedFrom":subQ0}),1.0]])]});}
            var Q36;
            {var subQ0=sQuery(id+"F0.wireOp",EDGE,"E59.MirrorCS");Q36=makeQuery(id+"F0.imprint","IMPRINT",FACE,{"disambiguationData":[TD([[makeQuery(id+"F0.imprint","IMPRINT",EDGE,{"derivedFrom":subQ0}),1.0]])]});}
            var Q37;
            {var subQ0=sQuery(id+"F0.wireOp",EDGE,"E57.MirrorCS");Q37=makeQuery(id+"F0.imprint","IMPRINT",FACE,{"disambiguationData":[TD([[makeQuery(id+"F0.imprint","IMPRINT",EDGE,{"derivedFrom":subQ0}),1.0]])]});}
            var Q38;
            {var subQ0=sQuery(id+"F0.wireOp",EDGE,"E41.MirrorCS");Q38=makeQuery(id+"F0.imprint","IMPRINT",FACE,{"disambiguationData":[TD([[makeQuery(id+"F0.imprint","IMPRINT",EDGE,{"derivedFrom":subQ0}),1.0]])]});}
            var Q39;
            {var subQ0=sQuery(id+"F0.wireOp",EDGE,"E56.MirrorCS");Q39=makeQuery(id+"F0.imprint","IMPRINT",FACE,{"disambiguationData":[TD([[makeQuery(id+"F0.imprint","IMPRINT",EDGE,{"derivedFrom":subQ0}),-1.0]])]});}
            var Q40;
            {var subQ0=sQuery(id+"F0.wireOp",EDGE,"E46.MirrorCS");Q40=makeQuery(id+"F0.imprint","IMPRINT",FACE,{"disambiguationData":[TD([[makeQuery(id+"F0.imprint","IMPRINT",EDGE,{"derivedFrom":subQ0}),1.0]])]});}
            var Q41;
            {var subQ0=sQuery(id+"F0.wireOp",EDGE,"E52.MirrorCS");Q41=makeQuery(id+"F0.imprint","IMPRINT",FACE,{"disambiguationData":[TD([[makeQuery(id+"F0.imprint","IMPRINT",EDGE,{"derivedFrom":subQ0}),1.0]])]});}
            var Q42;
            {var subQ58=sQuery(id+"F0.wireOp",EDGE,"E128");Q42=makeQuery(id+"F0.imprint","IMPRINT",FACE,{"disambiguationData":[TD([[makeQuery(id+"F0.imprint","IMPRINT",EDGE,{"derivedFrom":subQ58}),1.0]])]});}
            var Q43;
            {var subQ0=sQuery(id+"F0.wireOp",EDGE,"E4");Q43=makeQuery(id+"F0.imprint","IMPRINT",FACE,{"disambiguationData":[TD([[makeQuery(id+"F0.imprint","IMPRINT",EDGE,{"derivedFrom":subQ0}),-1.0]])]});}
            var Q44;
            {var subQ0=sQuery(id+"F0.wireOp",EDGE,"E8.MirrorCS");Q44=makeQuery(id+"F0.imprint","IMPRINT",FACE,{"disambiguationData":[TD([[makeQuery(id+"F0.imprint","IMPRINT",EDGE,{"derivedFrom":subQ0}),1.0]])]});}
            var Q45;
            {var subQ0=sQuery(id+"F0.wireOp",EDGE,"E10.MirrorCS");Q45=makeQuery(id+"F0.imprint","IMPRINT",FACE,{"disambiguationData":[TD([[makeQuery(id+"F0.imprint","IMPRINT",EDGE,{"derivedFrom":subQ0}),1.0]])]});}
            var Q46;
            {var subQ0=sQuery(id+"F0.wireOp",EDGE,"E12.MirrorCS");Q46=makeQuery(id+"F0.imprint","IMPRINT",FACE,{"disambiguationData":[TD([[makeQuery(id+"F0.imprint","IMPRINT",EDGE,{"derivedFrom":subQ0}),1.0]])]});}
            var Q47;
            {var subQ0=sQuery(id+"F0.wireOp",EDGE,"E14.MirrorCS");Q47=makeQuery(id+"F0.imprint","IMPRINT",FACE,{"disambiguationData":[TD([[makeQuery(id+"F0.imprint","IMPRINT",EDGE,{"derivedFrom":subQ0}),1.0]])]});}
            var Q48;
            {var subQ0=sQuery(id+"F0.wireOp",EDGE,"E16.MirrorCS");Q48=makeQuery(id+"F0.imprint","IMPRINT",FACE,{"disambiguationData":[TD([[makeQuery(id+"F0.imprint","IMPRINT",EDGE,{"derivedFrom":subQ0}),1.0]])]});}
            var Q49;
            {var subQ0=sQuery(id+"F0.wireOp",EDGE,"E18.MirrorCS");Q49=makeQuery(id+"F0.imprint","IMPRINT",FACE,{"disambiguationData":[TD([[makeQuery(id+"F0.imprint","IMPRINT",EDGE,{"derivedFrom":subQ0}),-1.0]])]});}
            var Q50;
            {var subQ0=sQuery(id+"F0.wireOp",EDGE,"E20.MirrorCS");Q50=makeQuery(id+"F0.imprint","IMPRINT",FACE,{"disambiguationData":[TD([[makeQuery(id+"F0.imprint","IMPRINT",EDGE,{"derivedFrom":subQ0}),1.0]])]});}
            var Q51;
            {var subQ0=sQuery(id+"F0.wireOp",EDGE,"E22.MirrorCS");Q51=makeQuery(id+"F0.imprint","IMPRINT",FACE,{"disambiguationData":[TD([[makeQuery(id+"F0.imprint","IMPRINT",EDGE,{"derivedFrom":subQ0}),1.0]])]});}
            var Q52;
            {var subQ5=sQuery(id+"F0.wireOp",EDGE,"E244");Q52=makeQuery(id+"F0.imprint","IMPRINT",FACE,{"disambiguationData":[TD([[makeQuery(id+"F0.imprint","IMPRINT",EDGE,{"derivedFrom":subQ5}),1.0]])]});}
            var Q53;
            {var subQ0=sQuery(id+"F0.wireOp",EDGE,"E6.8.0.1");Q53=makeQuery(id+"F0.imprint","IMPRINT",FACE,{"disambiguationData":[TD([[makeQuery(id+"F0.imprint","IMPRINT",EDGE,{"derivedFrom":subQ0}),1.0]])]});}
            var Q54;
            {var subQ0=sQuery(id+"F0.wireOp",EDGE,"E6.7.0.0");Q54=makeQuery(id+"F0.imprint","IMPRINT",FACE,{"disambiguationData":[TD([[makeQuery(id+"F0.imprint","IMPRINT",EDGE,{"derivedFrom":subQ0}),-1.0]])]});}
            var Q55;
            {var subQ0=sQuery(id+"F0.wireOp",EDGE,"E6.6.0.0");Q55=makeQuery(id+"F0.imprint","IMPRINT",FACE,{"disambiguationData":[TD([[makeQuery(id+"F0.imprint","IMPRINT",EDGE,{"derivedFrom":subQ0}),-1.0]])]});}
            var Q56;
            {var subQ0=sQuery(id+"F0.wireOp",EDGE,"E6.5.0.0");Q56=makeQuery(id+"F0.imprint","IMPRINT",FACE,{"disambiguationData":[TD([[makeQuery(id+"F0.imprint","IMPRINT",EDGE,{"derivedFrom":subQ0}),-1.0]])]});}
            var Q57;
            {var subQ0=sQuery(id+"F0.wireOp",EDGE,"E6.4.0.0");Q57=makeQuery(id+"F0.imprint","IMPRINT",FACE,{"disambiguationData":[TD([[makeQuery(id+"F0.imprint","IMPRINT",EDGE,{"derivedFrom":subQ0}),-1.0]])]});}
            var Q58;
            {var subQ0=sQuery(id+"F0.wireOp",EDGE,"E6.3.0.0");Q58=makeQuery(id+"F0.imprint","IMPRINT",FACE,{"disambiguationData":[TD([[makeQuery(id+"F0.imprint","IMPRINT",EDGE,{"derivedFrom":subQ0}),-1.0]])]});}
            var Q59;
            {var subQ0=sQuery(id+"F0.wireOp",EDGE,"E6.2.0.0");Q59=makeQuery(id+"F0.imprint","IMPRINT",FACE,{"disambiguationData":[TD([[makeQuery(id+"F0.imprint","IMPRINT",EDGE,{"derivedFrom":subQ0}),-1.0]])]});}
            var Q60;
            {var subQ0=sQuery(id+"F0.wireOp",EDGE,"E6.1.0.0");Q60=makeQuery(id+"F0.imprint","IMPRINT",FACE,{"disambiguationData":[TD([[makeQuery(id+"F0.imprint","IMPRINT",EDGE,{"derivedFrom":subQ0}),-1.0]])]});}
            var Q61;
            {var subQ0=sQuery(id+"F0.wireOp",EDGE,"E132.MirrorCS");Q61=makeQuery(id+"F0.imprint","IMPRINT",FACE,{"disambiguationData":[TD([[makeQuery(id+"F0.imprint","IMPRINT",EDGE,{"derivedFrom":subQ0}),1.0]])]});}
            var Q62;
            {var subQ0=sQuery(id+"F0.wireOp",EDGE,"E134.1.0.0");Q62=makeQuery(id+"F0.imprint","IMPRINT",FACE,{"disambiguationData":[TD([[makeQuery(id+"F0.imprint","IMPRINT",EDGE,{"derivedFrom":subQ0}),1.0]])]});}
            var Q63;
            {var subQ0=sQuery(id+"F0.wireOp",EDGE,"E134.2.0.0");Q63=makeQuery(id+"F0.imprint","IMPRINT",FACE,{"disambiguationData":[TD([[makeQuery(id+"F0.imprint","IMPRINT",EDGE,{"derivedFrom":subQ0}),1.0]])]});}
            var Q64;
            {var subQ0=sQuery(id+"F0.wireOp",EDGE,"E134.3.0.0");Q64=makeQuery(id+"F0.imprint","IMPRINT",FACE,{"disambiguationData":[TD([[makeQuery(id+"F0.imprint","IMPRINT",EDGE,{"derivedFrom":subQ0}),1.0]])]});}
            var Q65;
            {var subQ0=sQuery(id+"F0.wireOp",EDGE,"E134.4.0.0");Q65=makeQuery(id+"F0.imprint","IMPRINT",FACE,{"disambiguationData":[TD([[makeQuery(id+"F0.imprint","IMPRINT",EDGE,{"derivedFrom":subQ0}),1.0]])]});}
            var Q66;
            {var subQ2=sQuery(id+"F0.wireOp",EDGE,"E133.5.0.1");Q66=makeQuery(id+"F0.imprint","IMPRINT",FACE,{"disambiguationData":[TD([[makeQuery(id+"F0.imprint","IMPRINT",EDGE,{"derivedFrom":subQ2}),-1.0]])]});}
            var Q67;
            {var subQ0=sQuery(id+"F0.wireOp",EDGE,"E133.4.0.0");Q67=makeQuery(id+"F0.imprint","IMPRINT",FACE,{"disambiguationData":[TD([[makeQuery(id+"F0.imprint","IMPRINT",EDGE,{"derivedFrom":subQ0}),1.0]])]});}
            var Q68;
            {var subQ0=sQuery(id+"F0.wireOp",EDGE,"E133.3.0.0");Q68=makeQuery(id+"F0.imprint","IMPRINT",FACE,{"disambiguationData":[TD([[makeQuery(id+"F0.imprint","IMPRINT",EDGE,{"derivedFrom":subQ0}),1.0]])]});}
            var Q69;
            {var subQ0=sQuery(id+"F0.wireOp",EDGE,"E133.2.0.0");Q69=makeQuery(id+"F0.imprint","IMPRINT",FACE,{"disambiguationData":[TD([[makeQuery(id+"F0.imprint","IMPRINT",EDGE,{"derivedFrom":subQ0}),1.0]])]});}
            var Q70;
            {var subQ0=sQuery(id+"F0.wireOp",EDGE,"E133.1.0.0");Q70=makeQuery(id+"F0.imprint","IMPRINT",FACE,{"disambiguationData":[TD([[makeQuery(id+"F0.imprint","IMPRINT",EDGE,{"derivedFrom":subQ0}),1.0]])]});}
            var Q71;
            {var subQ0=sQuery(id+"F0.wireOp",EDGE,"E128");Q71=makeQuery(id+"F0.imprint","IMPRINT",FACE,{"disambiguationData":[TD([[makeQuery(id+"F0.imprint","IMPRINT",EDGE,{"derivedFrom":subQ0}),-1.0]])]});}
            var Q72;
            {var subQ0=sQuery(id+"F0.wireOp",EDGE,"E221.MirrorCS");Q72=makeQuery(id+"F0.imprint","IMPRINT",FACE,{"disambiguationData":[TD([[makeQuery(id+"F0.imprint","IMPRINT",EDGE,{"derivedFrom":subQ0}),-1.0]])]});}
            var Q73;
            {var subQ0=sQuery(id+"F0.wireOp",EDGE,"E223.MirrorCS");Q73=makeQuery(id+"F0.imprint","IMPRINT",FACE,{"disambiguationData":[TD([[makeQuery(id+"F0.imprint","IMPRINT",EDGE,{"derivedFrom":subQ0}),-1.0]])]});}
            var Q74;
            {var subQ0=sQuery(id+"F0.wireOp",EDGE,"E225.MirrorCS");Q74=makeQuery(id+"F0.imprint","IMPRINT",FACE,{"disambiguationData":[TD([[makeQuery(id+"F0.imprint","IMPRINT",EDGE,{"derivedFrom":subQ0}),-1.0]])]});}
            var Q75;
            {var subQ0=sQuery(id+"F0.wireOp",EDGE,"E227.MirrorCS");Q75=makeQuery(id+"F0.imprint","IMPRINT",FACE,{"disambiguationData":[TD([[makeQuery(id+"F0.imprint","IMPRINT",EDGE,{"derivedFrom":subQ0}),-1.0]])]});}
            var Q76;
            {var subQ0=sQuery(id+"F0.wireOp",EDGE,"E229.MirrorCS");Q76=makeQuery(id+"F0.imprint","IMPRINT",FACE,{"disambiguationData":[TD([[makeQuery(id+"F0.imprint","IMPRINT",EDGE,{"derivedFrom":subQ0}),-1.0]])]});}
            var Q77;
            Q77=makeQuery(id+"F0.imprint","IMPRINT",FACE,{"disambiguationData":[TD([[makeQuery(id+"F0.imprint","IMPRINT",EDGE,{"derivedFrom":sQuery(id+"F0.wireOp",EDGE,"E31.MirrorCS")}),-1.0]])]});
            var Q78;
            {var subQ0=sQuery(id+"F0.wireOp",EDGE,"E241.MirrorCS");Q78=makeQuery(id+"F0.imprint","IMPRINT",FACE,{"disambiguationData":[TD([[makeQuery(id+"F0.imprint","IMPRINT",EDGE,{"derivedFrom":subQ0}),-1.0]])]});}
            var Q79;
            {var subQ0=sQuery(id+"F0.wireOp",EDGE,"E239.MirrorCS");Q79=makeQuery(id+"F0.imprint","IMPRINT",FACE,{"disambiguationData":[TD([[makeQuery(id+"F0.imprint","IMPRINT",EDGE,{"derivedFrom":subQ0}),-1.0]])]});}
            var Q80;
            {var subQ0=sQuery(id+"F0.wireOp",EDGE,"E237.MirrorCS");Q80=makeQuery(id+"F0.imprint","IMPRINT",FACE,{"disambiguationData":[TD([[makeQuery(id+"F0.imprint","IMPRINT",EDGE,{"derivedFrom":subQ0}),-1.0]])]});}
            var Q81;
            {var subQ0=sQuery(id+"F0.wireOp",EDGE,"E235.MirrorCS");Q81=makeQuery(id+"F0.imprint","IMPRINT",FACE,{"disambiguationData":[TD([[makeQuery(id+"F0.imprint","IMPRINT",EDGE,{"derivedFrom":subQ0}),-1.0]])]});}
            var Q82;
            {var subQ0=sQuery(id+"F0.wireOp",EDGE,"E233.MirrorCS");Q82=makeQuery(id+"F0.imprint","IMPRINT",FACE,{"disambiguationData":[TD([[makeQuery(id+"F0.imprint","IMPRINT",EDGE,{"derivedFrom":subQ0}),-1.0]])]});}
            var Q83;
            {var subQ2=sQuery(id+"F0.wireOp",EDGE,"E231.MirrorCS");Q83=makeQuery(id+"F0.imprint","IMPRINT",FACE,{"disambiguationData":[TD([[makeQuery(id+"F0.imprint","IMPRINT",EDGE,{"derivedFrom":subQ2}),-1.0]])]});}
            var Q84;
            Q84=makeQuery(id+"F0.imprint","IMPRINT",FACE,{"disambiguationData":[TD([[makeQuery(id+"F0.imprint","IMPRINT",EDGE,{"derivedFrom":sQuery(id+"F0.wireOp",EDGE,"E136.MirrorCS")}),1.0]])]});
            var Q85;
            {var subQ4=sQuery(id+"F0.wireOp",EDGE,"E196.MirrorCS");Q85=makeQuery(id+"F0.imprint","IMPRINT",FACE,{"disambiguationData":[TD([[makeQuery(id+"F0.imprint","IMPRINT",EDGE,{"derivedFrom":subQ4}),1.0]])]});}
            var Q86;
            {var subQ3=sQuery(id+"F0.wireOp",EDGE,"E142.MirrorCS");Q86=makeQuery(id+"F0.imprint","IMPRINT",FACE,{"disambiguationData":[TD([[makeQuery(id+"F0.imprint","IMPRINT",EDGE,{"derivedFrom":subQ3}),-1.0]])]});}
            var Q87;
            {var subQ5=sQuery(id+"F0.wireOp",EDGE,"E88.MirrorCS");Q87=makeQuery(id+"F0.imprint","IMPRINT",FACE,{"disambiguationData":[TD([[makeQuery(id+"F0.imprint","IMPRINT",EDGE,{"derivedFrom":subQ5}),1.0]])]});}
            var Q88;
            {var subQ3=sQuery(id+"F0.wireOp",EDGE,"E166.MirrorCS");Q88=makeQuery(id+"F0.imprint","IMPRINT",FACE,{"disambiguationData":[TD([[makeQuery(id+"F0.imprint","IMPRINT",EDGE,{"derivedFrom":subQ3}),1.0]])]});}
            var Q89;
            {var subQ3=sQuery(id+"F0.wireOp",EDGE,"E247");Q89=makeQuery(id+"F0.imprint","IMPRINT",FACE,{"disambiguationData":[TD([[makeQuery(id+"F0.imprint","IMPRINT",EDGE,{"derivedFrom":subQ3}),-1.0]])]});}
            var Q90;
            {var subQ0=sQuery(id+"F0.wireOp",EDGE,"E157.MirrorCS");Q90=makeQuery(id+"F0.imprint","IMPRINT",FACE,{"disambiguationData":[TD([[makeQuery(id+"F0.imprint","IMPRINT",EDGE,{"derivedFrom":subQ0}),1.0]])]});}
            var Q91;
            {var subQ0=sQuery(id+"F0.wireOp",EDGE,"E155.MirrorCS");Q91=makeQuery(id+"F0.imprint","IMPRINT",FACE,{"disambiguationData":[TD([[makeQuery(id+"F0.imprint","IMPRINT",EDGE,{"derivedFrom":subQ0}),1.0]])]});}
            var Q92;
            {var subQ0=sQuery(id+"F0.wireOp",EDGE,"E153.MirrorCS");Q92=makeQuery(id+"F0.imprint","IMPRINT",FACE,{"disambiguationData":[TD([[makeQuery(id+"F0.imprint","IMPRINT",EDGE,{"derivedFrom":subQ0}),1.0]])]});}
            var Q93;
            {var subQ0=sQuery(id+"F0.wireOp",EDGE,"E151.MirrorCS");Q93=makeQuery(id+"F0.imprint","IMPRINT",FACE,{"disambiguationData":[TD([[makeQuery(id+"F0.imprint","IMPRINT",EDGE,{"derivedFrom":subQ0}),1.0]])]});}
            var Q94;
            {var subQ0=sQuery(id+"F0.wireOp",EDGE,"E149.MirrorCS");Q94=makeQuery(id+"F0.imprint","IMPRINT",FACE,{"disambiguationData":[TD([[makeQuery(id+"F0.imprint","IMPRINT",EDGE,{"derivedFrom":subQ0}),1.0]])]});}
            var Q95;
            {var subQ0=sQuery(id+"F0.wireOp",EDGE,"E147.MirrorCS");Q95=makeQuery(id+"F0.imprint","IMPRINT",FACE,{"disambiguationData":[TD([[makeQuery(id+"F0.imprint","IMPRINT",EDGE,{"derivedFrom":subQ0}),1.0]])]});}
            var Q96;
            {var subQ0=sQuery(id+"F0.wireOp",EDGE,"E145.MirrorCS");Q96=makeQuery(id+"F0.imprint","IMPRINT",FACE,{"disambiguationData":[TD([[makeQuery(id+"F0.imprint","IMPRINT",EDGE,{"derivedFrom":subQ0}),1.0]])]});}
            var Q97;
            {var subQ0=sQuery(id+"F0.wireOp",EDGE,"E143.MirrorCS");Q97=makeQuery(id+"F0.imprint","IMPRINT",FACE,{"disambiguationData":[TD([[makeQuery(id+"F0.imprint","IMPRINT",EDGE,{"derivedFrom":subQ0}),1.0]])]});}
            var Q98;
            {var subQ0=sQuery(id+"F0.wireOp",EDGE,"E164.MirrorCS");Q98=makeQuery(id+"F0.imprint","IMPRINT",FACE,{"disambiguationData":[TD([[makeQuery(id+"F0.imprint","IMPRINT",EDGE,{"derivedFrom":subQ0}),1.0]])]});}
            var Q99;
            {var subQ0=sQuery(id+"F0.wireOp",EDGE,"E162.MirrorCS");Q99=makeQuery(id+"F0.imprint","IMPRINT",FACE,{"disambiguationData":[TD([[makeQuery(id+"F0.imprint","IMPRINT",EDGE,{"derivedFrom":subQ0}),1.0]])]});}
            var Q100;
            {var subQ0=sQuery(id+"F0.wireOp",EDGE,"E160.MirrorCS");Q100=makeQuery(id+"F0.imprint","IMPRINT",FACE,{"disambiguationData":[TD([[makeQuery(id+"F0.imprint","IMPRINT",EDGE,{"derivedFrom":subQ0}),1.0]])]});}
            var Q101;
            {var subQ0=sQuery(id+"F0.wireOp",EDGE,"E158.MirrorCS");Q101=makeQuery(id+"F0.imprint","IMPRINT",FACE,{"disambiguationData":[TD([[makeQuery(id+"F0.imprint","IMPRINT",EDGE,{"derivedFrom":subQ0}),1.0]])]});}
            var Q102;
            {var subQ0=sQuery(id+"F0.wireOp",EDGE,"E160.MirrorCS");Q102=makeQuery(id+"F0.imprint","IMPRINT",FACE,{"disambiguationData":[TD([[makeQuery(id+"F0.imprint","IMPRINT",EDGE,{"derivedFrom":subQ0}),1.0]])]});}
            var Q103;
            {var subQ5=sQuery(id+"F0.wireOp",EDGE,"E249");Q103=makeQuery(id+"F0.imprint","IMPRINT",FACE,{"disambiguationData":[TD([[makeQuery(id+"F0.imprint","IMPRINT",EDGE,{"derivedFrom":subQ5}),1.0]])]});}
            var Q104;
            {var subQ0=sQuery(id+"F0.wireOp",EDGE,"E73.MirrorCS");Q104=makeQuery(id+"F0.imprint","IMPRINT",FACE,{"disambiguationData":[TD([[makeQuery(id+"F0.imprint","IMPRINT",EDGE,{"derivedFrom":subQ0}),-1.0]])]});}
            var Q105;
            {var subQ0=sQuery(id+"F0.wireOp",EDGE,"E74.MirrorCS");Q105=makeQuery(id+"F0.imprint","IMPRINT",FACE,{"disambiguationData":[TD([[makeQuery(id+"F0.imprint","IMPRINT",EDGE,{"derivedFrom":subQ0}),1.0]])]});}
            var Q106;
            {var subQ0=sQuery(id+"F0.wireOp",EDGE,"E76.MirrorCS");Q106=makeQuery(id+"F0.imprint","IMPRINT",FACE,{"disambiguationData":[TD([[makeQuery(id+"F0.imprint","IMPRINT",EDGE,{"derivedFrom":subQ0}),1.0]])]});}
            var Q107;
            {var subQ0=sQuery(id+"F0.wireOp",EDGE,"E78.MirrorCS");Q107=makeQuery(id+"F0.imprint","IMPRINT",FACE,{"disambiguationData":[TD([[makeQuery(id+"F0.imprint","IMPRINT",EDGE,{"derivedFrom":subQ0}),1.0]])]});}
            var Q108;
            {var subQ0=sQuery(id+"F0.wireOp",EDGE,"E80.MirrorCS");Q108=makeQuery(id+"F0.imprint","IMPRINT",FACE,{"disambiguationData":[TD([[makeQuery(id+"F0.imprint","IMPRINT",EDGE,{"derivedFrom":subQ0}),1.0]])]});}
            var Q109;
            {var subQ0=sQuery(id+"F0.wireOp",EDGE,"E82.MirrorCS");Q109=makeQuery(id+"F0.imprint","IMPRINT",FACE,{"disambiguationData":[TD([[makeQuery(id+"F0.imprint","IMPRINT",EDGE,{"derivedFrom":subQ0}),1.0]])]});}
            var Q110;
            {var subQ0=sQuery(id+"F0.wireOp",EDGE,"E84.MirrorCS");Q110=makeQuery(id+"F0.imprint","IMPRINT",FACE,{"disambiguationData":[TD([[makeQuery(id+"F0.imprint","IMPRINT",EDGE,{"derivedFrom":subQ0}),1.0]])]});}
            var Q111;
            {var subQ0=sQuery(id+"F0.wireOp",EDGE,"E86.MirrorCS");Q111=makeQuery(id+"F0.imprint","IMPRINT",FACE,{"disambiguationData":[TD([[makeQuery(id+"F0.imprint","IMPRINT",EDGE,{"derivedFrom":subQ0}),1.0]])]});}
            var Q112;
            {var subQ5=sQuery(id+"F0.wireOp",EDGE,"E93.MirrorCS");Q112=makeQuery(id+"F0.imprint","IMPRINT",FACE,{"disambiguationData":[TD([[makeQuery(id+"F0.imprint","IMPRINT",EDGE,{"derivedFrom":subQ5}),-1.0]])]});}
            var Q113;
            {var subQ0=sQuery(id+"F0.wireOp",EDGE,"E94.MirrorCS");Q113=makeQuery(id+"F0.imprint","IMPRINT",FACE,{"disambiguationData":[TD([[makeQuery(id+"F0.imprint","IMPRINT",EDGE,{"derivedFrom":subQ0}),1.0]])]});}
            var Q114;
            {var subQ0=sQuery(id+"F0.wireOp",EDGE,"E96.MirrorCS");Q114=makeQuery(id+"F0.imprint","IMPRINT",FACE,{"disambiguationData":[TD([[makeQuery(id+"F0.imprint","IMPRINT",EDGE,{"derivedFrom":subQ0}),1.0]])]});}
            var Q115;
            {var subQ0=sQuery(id+"F0.wireOp",EDGE,"E98.MirrorCS");Q115=makeQuery(id+"F0.imprint","IMPRINT",FACE,{"disambiguationData":[TD([[makeQuery(id+"F0.imprint","IMPRINT",EDGE,{"derivedFrom":subQ0}),1.0]])]});}
            var Q116;
            {var subQ0=sQuery(id+"F0.wireOp",EDGE,"E100.MirrorCS");Q116=makeQuery(id+"F0.imprint","IMPRINT",FACE,{"disambiguationData":[TD([[makeQuery(id+"F0.imprint","IMPRINT",EDGE,{"derivedFrom":subQ0}),1.0]])]});}
            var Q117;
            {var subQ0=sQuery(id+"F0.wireOp",EDGE,"E172.MirrorCS");Q117=makeQuery(id+"F0.imprint","IMPRINT",FACE,{"disambiguationData":[TD([[makeQuery(id+"F0.imprint","IMPRINT",EDGE,{"derivedFrom":subQ0}),1.0]])]});}
            var Q118;
            {var subQ0=sQuery(id+"F0.wireOp",EDGE,"E174.MirrorCS");Q118=makeQuery(id+"F0.imprint","IMPRINT",FACE,{"disambiguationData":[TD([[makeQuery(id+"F0.imprint","IMPRINT",EDGE,{"derivedFrom":subQ0}),1.0]])]});}
            var Q119;
            {var subQ0=sQuery(id+"F0.wireOp",EDGE,"E176.MirrorCS");Q119=makeQuery(id+"F0.imprint","IMPRINT",FACE,{"disambiguationData":[TD([[makeQuery(id+"F0.imprint","IMPRINT",EDGE,{"derivedFrom":subQ0}),1.0]])]});}
            var Q120;
            {var subQ0=sQuery(id+"F0.wireOp",EDGE,"E178.MirrorCS");Q120=makeQuery(id+"F0.imprint","IMPRINT",FACE,{"disambiguationData":[TD([[makeQuery(id+"F0.imprint","IMPRINT",EDGE,{"derivedFrom":subQ0}),1.0]])]});}
            var Q121;
            {var subQ0=sQuery(id+"F0.wireOp",EDGE,"E180.MirrorCS");Q121=makeQuery(id+"F0.imprint","IMPRINT",FACE,{"disambiguationData":[TD([[makeQuery(id+"F0.imprint","IMPRINT",EDGE,{"derivedFrom":subQ0}),1.0]])]});}
            var Q122;
            {var subQ0=sQuery(id+"F0.wireOp",EDGE,"E182.MirrorCS");Q122=makeQuery(id+"F0.imprint","IMPRINT",FACE,{"disambiguationData":[TD([[makeQuery(id+"F0.imprint","IMPRINT",EDGE,{"derivedFrom":subQ0}),1.0]])]});}
            var Q123;
            {var subQ0=sQuery(id+"F0.wireOp",EDGE,"E184.MirrorCS");Q123=makeQuery(id+"F0.imprint","IMPRINT",FACE,{"disambiguationData":[TD([[makeQuery(id+"F0.imprint","IMPRINT",EDGE,{"derivedFrom":subQ0}),1.0]])]});}
            var Q124;
            {var subQ0=sQuery(id+"F0.wireOp",EDGE,"E186.MirrorCS");Q124=makeQuery(id+"F0.imprint","IMPRINT",FACE,{"disambiguationData":[TD([[makeQuery(id+"F0.imprint","IMPRINT",EDGE,{"derivedFrom":subQ0}),1.0]])]});}
            var Q125;
            {var subQ0=sQuery(id+"F0.wireOp",EDGE,"E188.MirrorCS");Q125=makeQuery(id+"F0.imprint","IMPRINT",FACE,{"disambiguationData":[TD([[makeQuery(id+"F0.imprint","IMPRINT",EDGE,{"derivedFrom":subQ0}),1.0]])]});}
            var Q126;
            {var subQ0=sQuery(id+"F0.wireOp",EDGE,"E190.MirrorCS");Q126=makeQuery(id+"F0.imprint","IMPRINT",FACE,{"disambiguationData":[TD([[makeQuery(id+"F0.imprint","IMPRINT",EDGE,{"derivedFrom":subQ0}),1.0]])]});}
            var Q127;
            {var subQ2=sQuery(id+"F0.wireOp",EDGE,"E192.MirrorCS");Q127=makeQuery(id+"F0.imprint","IMPRINT",FACE,{"disambiguationData":[TD([[makeQuery(id+"F0.imprint","IMPRINT",EDGE,{"derivedFrom":subQ2}),1.0]])]});}
            var Q128;
            {var subQ0=sQuery(id+"F0.wireOp",EDGE,"E197.MirrorCS");Q128=makeQuery(id+"F0.imprint","IMPRINT",FACE,{"disambiguationData":[TD([[makeQuery(id+"F0.imprint","IMPRINT",EDGE,{"derivedFrom":subQ0}),-1.0]])]});}
            var Q129;
            {var subQ0=sQuery(id+"F0.wireOp",EDGE,"E199.MirrorCS");Q129=makeQuery(id+"F0.imprint","IMPRINT",FACE,{"disambiguationData":[TD([[makeQuery(id+"F0.imprint","IMPRINT",EDGE,{"derivedFrom":subQ0}),-1.0]])]});}
            var Q130;
            {var subQ0=sQuery(id+"F0.wireOp",EDGE,"E201.MirrorCS");Q130=makeQuery(id+"F0.imprint","IMPRINT",FACE,{"disambiguationData":[TD([[makeQuery(id+"F0.imprint","IMPRINT",EDGE,{"derivedFrom":subQ0}),-1.0]])]});}
            var Q131;
            {var subQ0=sQuery(id+"F0.wireOp",EDGE,"E203.MirrorCS");Q131=makeQuery(id+"F0.imprint","IMPRINT",FACE,{"disambiguationData":[TD([[makeQuery(id+"F0.imprint","IMPRINT",EDGE,{"derivedFrom":subQ0}),-1.0]])]});}
            var Q132;
            {var subQ0=sQuery(id+"F0.wireOp",EDGE,"E205.MirrorCS");Q132=makeQuery(id+"F0.imprint","IMPRINT",FACE,{"disambiguationData":[TD([[makeQuery(id+"F0.imprint","IMPRINT",EDGE,{"derivedFrom":subQ0}),-1.0]])]});}
            var Q133;
            {var subQ0=sQuery(id+"F0.wireOp",EDGE,"E207.MirrorCS");Q133=makeQuery(id+"F0.imprint","IMPRINT",FACE,{"disambiguationData":[TD([[makeQuery(id+"F0.imprint","IMPRINT",EDGE,{"derivedFrom":subQ0}),-1.0]])]});}
            var Q134;
            {var subQ0=sQuery(id+"F0.wireOp",EDGE,"E209.MirrorCS");Q134=makeQuery(id+"F0.imprint","IMPRINT",FACE,{"disambiguationData":[TD([[makeQuery(id+"F0.imprint","IMPRINT",EDGE,{"derivedFrom":subQ0}),-1.0]])]});}
            var Q135;
            {var subQ0=sQuery(id+"F0.wireOp",EDGE,"E216.MirrorCS");Q135=makeQuery(id+"F0.imprint","IMPRINT",FACE,{"disambiguationData":[TD([[makeQuery(id+"F0.imprint","IMPRINT",EDGE,{"derivedFrom":subQ0}),1.0]])]});}
            var Q136;
            {var subQ0=sQuery(id+"F0.wireOp",EDGE,"E214.MirrorCS");Q136=makeQuery(id+"F0.imprint","IMPRINT",FACE,{"disambiguationData":[TD([[makeQuery(id+"F0.imprint","IMPRINT",EDGE,{"derivedFrom":subQ0}),1.0]])]});}
            var Q137;
            {var subQ0=sQuery(id+"F0.wireOp",EDGE,"E212.MirrorCS");Q137=makeQuery(id+"F0.imprint","IMPRINT",FACE,{"disambiguationData":[TD([[makeQuery(id+"F0.imprint","IMPRINT",EDGE,{"derivedFrom":subQ0}),1.0]])]});}
            var Q138;
            {var subQ0=sQuery(id+"F0.wireOp",EDGE,"E210.MirrorCS");Q138=makeQuery(id+"F0.imprint","IMPRINT",FACE,{"disambiguationData":[TD([[makeQuery(id+"F0.imprint","IMPRINT",EDGE,{"derivedFrom":subQ0}),1.0]])]});}
            var Q139;
            {var subQ2=sQuery(id+"F0.wireOp",EDGE,"E192.MirrorCS");Q139=makeQuery(id+"F0.imprint","IMPRINT",FACE,{"disambiguationData":[TD([[makeQuery(id+"F0.imprint","IMPRINT",EDGE,{"derivedFrom":subQ2}),1.0]])]});}
            var Q140;
            Q140=makeQuery(id+"F0.imprint","IMPRINT",FACE,{"disambiguationData":[TD([[makeQuery(id+"F0.imprint","IMPRINT",EDGE,{"derivedFrom":sQuery(id+"F0.wireOp",EDGE,"E330.bottom")}),1.0]])]});
            var Q141;
            {var subQ10=sQuery(id+"F0.wireOp",EDGE,"E355");var subQ41=sQuery(id+"F0.wireOp",EDGE,"E358");var subQ48=makeQuery(id+"F0.imprint","INTERSECT",VERTEX,{"derivedFrom":[subQ10,subQ41]});Q141=makeQuery(id+"F0.imprint","IMPRINT",FACE,{"disambiguationData":[TD([[makeQuery(id+"F0.imprint","IMPRINT",EDGE,{"disambiguationData":[TD([[subQ48,-1.0]])],"derivedFrom":subQ10}),-1.0]])]});}
            var Q142;
            {var subQ0=sQuery(id+"F0.wireOp",EDGE,"E364.MirrorCS");Q142=makeQuery(id+"F0.imprint","IMPRINT",FACE,{"disambiguationData":[TD([[makeQuery(id+"F0.imprint","IMPRINT",EDGE,{"derivedFrom":subQ0}),1.0]])]});}
            var Q143;
            {var subQ0=sQuery(id+"F0.wireOp",EDGE,"E360");Q143=makeQuery(id+"F0.imprint","IMPRINT",FACE,{"disambiguationData":[TD([[makeQuery(id+"F0.imprint","IMPRINT",EDGE,{"derivedFrom":subQ0}),-1.0]])]});}
            var Q144;
            {var subQ0=sQuery(id+"F0.wireOp",EDGE,"E376.MirrorCS");Q144=makeQuery(id+"F0.imprint","IMPRINT",FACE,{"disambiguationData":[TD([[makeQuery(id+"F0.imprint","IMPRINT",EDGE,{"derivedFrom":subQ0}),1.0]])]});}
            var Q145;
            {var subQ0=sQuery(id+"F0.wireOp",EDGE,"E378.MirrorCS");Q145=makeQuery(id+"F0.imprint","IMPRINT",FACE,{"disambiguationData":[TD([[makeQuery(id+"F0.imprint","IMPRINT",EDGE,{"derivedFrom":subQ0}),1.0]])]});}
            var Q146;
            {var subQ0=sQuery(id+"F0.wireOp",EDGE,"E371.1.0.0");Q146=makeQuery(id+"F0.imprint","IMPRINT",FACE,{"disambiguationData":[TD([[makeQuery(id+"F0.imprint","IMPRINT",EDGE,{"derivedFrom":subQ0}),-1.0]])]});}
            var Q147;
            {var subQ0=sQuery(id+"F0.wireOp",EDGE,"E371.2.0.0");Q147=makeQuery(id+"F0.imprint","IMPRINT",FACE,{"disambiguationData":[TD([[makeQuery(id+"F0.imprint","IMPRINT",EDGE,{"derivedFrom":subQ0}),-1.0]])]});}
            var Q148;
            {var subQ0=sQuery(id+"F0.wireOp",EDGE,"E371.3.0.0");Q148=makeQuery(id+"F0.imprint","IMPRINT",FACE,{"disambiguationData":[TD([[makeQuery(id+"F0.imprint","IMPRINT",EDGE,{"derivedFrom":subQ0}),-1.0]])]});}
            var Q149;
            {var subQ0=sQuery(id+"F0.wireOp",EDGE,"E371.4.0.0");Q149=makeQuery(id+"F0.imprint","IMPRINT",FACE,{"disambiguationData":[TD([[makeQuery(id+"F0.imprint","IMPRINT",EDGE,{"derivedFrom":subQ0}),-1.0]])]});}
            var Q150;
            {var subQ0=sQuery(id+"F0.wireOp",EDGE,"E371.5.0.0");Q150=makeQuery(id+"F0.imprint","IMPRINT",FACE,{"disambiguationData":[TD([[makeQuery(id+"F0.imprint","IMPRINT",EDGE,{"derivedFrom":subQ0}),-1.0]])]});}
            var Q151;
            {var subQ0=sQuery(id+"F0.wireOp",EDGE,"E371.6.0.0");Q151=makeQuery(id+"F0.imprint","IMPRINT",FACE,{"disambiguationData":[TD([[makeQuery(id+"F0.imprint","IMPRINT",EDGE,{"derivedFrom":subQ0}),-1.0]])]});}
            var Q152;
            {var subQ0=sQuery(id+"F0.wireOp",EDGE,"E371.7.0.0");Q152=makeQuery(id+"F0.imprint","IMPRINT",FACE,{"disambiguationData":[TD([[makeQuery(id+"F0.imprint","IMPRINT",EDGE,{"derivedFrom":subQ0}),-1.0]])]});}
            var Q153;
            {var subQ0=sQuery(id+"F0.wireOp",EDGE,"E371.8.0.0");Q153=makeQuery(id+"F0.imprint","IMPRINT",FACE,{"disambiguationData":[TD([[makeQuery(id+"F0.imprint","IMPRINT",EDGE,{"derivedFrom":subQ0}),-1.0]])]});}
            var Q154;
            {var subQ0=sQuery(id+"F0.wireOp",EDGE,"E371.9.0.0");Q154=makeQuery(id+"F0.imprint","IMPRINT",FACE,{"disambiguationData":[TD([[makeQuery(id+"F0.imprint","IMPRINT",EDGE,{"derivedFrom":subQ0}),-1.0]])]});}
            var Q155;
            {var subQ0=sQuery(id+"F0.wireOp",EDGE,"E372.0.10.0");Q155=makeQuery(id+"F0.imprint","IMPRINT",FACE,{"disambiguationData":[TD([[makeQuery(id+"F0.imprint","IMPRINT",EDGE,{"derivedFrom":subQ0}),-1.0]])]});}
            var Q156;
            {var subQ0=sQuery(id+"F0.wireOp",EDGE,"E380.MirrorCS");Q156=makeQuery(id+"F0.imprint","IMPRINT",FACE,{"disambiguationData":[TD([[makeQuery(id+"F0.imprint","IMPRINT",EDGE,{"derivedFrom":subQ0}),1.0]])]});}
            var Q157;
            {var subQ0=sQuery(id+"F0.wireOp",EDGE,"E382.MirrorCS");Q157=makeQuery(id+"F0.imprint","IMPRINT",FACE,{"disambiguationData":[TD([[makeQuery(id+"F0.imprint","IMPRINT",EDGE,{"derivedFrom":subQ0}),1.0]])]});}
            var Q158;
            {var subQ0=sQuery(id+"F0.wireOp",EDGE,"E385.MirrorCS");Q158=makeQuery(id+"F0.imprint","IMPRINT",FACE,{"disambiguationData":[TD([[makeQuery(id+"F0.imprint","IMPRINT",EDGE,{"derivedFrom":subQ0}),1.0]])]});}
            var Q159;
            {var subQ0=sQuery(id+"F0.wireOp",EDGE,"E387.MirrorCS");Q159=makeQuery(id+"F0.imprint","IMPRINT",FACE,{"disambiguationData":[TD([[makeQuery(id+"F0.imprint","IMPRINT",EDGE,{"derivedFrom":subQ0}),1.0]])]});}
            var Q160;
            {var subQ0=sQuery(id+"F0.wireOp",EDGE,"E389.MirrorCS");Q160=makeQuery(id+"F0.imprint","IMPRINT",FACE,{"disambiguationData":[TD([[makeQuery(id+"F0.imprint","IMPRINT",EDGE,{"derivedFrom":subQ0}),1.0]])]});}
            var Q161;
            {var subQ0=sQuery(id+"F0.wireOp",EDGE,"E391.MirrorCS");Q161=makeQuery(id+"F0.imprint","IMPRINT",FACE,{"disambiguationData":[TD([[makeQuery(id+"F0.imprint","IMPRINT",EDGE,{"derivedFrom":subQ0}),1.0]])]});}
            var Q162;
            {var subQ0=sQuery(id+"F0.wireOp",EDGE,"E393.MirrorCS");Q162=makeQuery(id+"F0.imprint","IMPRINT",FACE,{"disambiguationData":[TD([[makeQuery(id+"F0.imprint","IMPRINT",EDGE,{"derivedFrom":subQ0}),-1.0]])]});}
            var Q163;
            {var subQ0=sQuery(id+"F0.wireOp",EDGE,"E370.0.10.0");Q163=makeQuery(id+"F0.imprint","IMPRINT",FACE,{"disambiguationData":[TD([[makeQuery(id+"F0.imprint","IMPRINT",EDGE,{"derivedFrom":subQ0}),1.0]])]});}
            var Q164;
            {var subQ0=sQuery(id+"F0.wireOp",EDGE,"E369.9.0.0");Q164=makeQuery(id+"F0.imprint","IMPRINT",FACE,{"disambiguationData":[TD([[makeQuery(id+"F0.imprint","IMPRINT",EDGE,{"derivedFrom":subQ0}),1.0]])]});}
            var Q165;
            {var subQ0=sQuery(id+"F0.wireOp",EDGE,"E369.8.0.0");Q165=makeQuery(id+"F0.imprint","IMPRINT",FACE,{"disambiguationData":[TD([[makeQuery(id+"F0.imprint","IMPRINT",EDGE,{"derivedFrom":subQ0}),1.0]])]});}
            var Q166;
            {var subQ0=sQuery(id+"F0.wireOp",EDGE,"E369.7.0.0");Q166=makeQuery(id+"F0.imprint","IMPRINT",FACE,{"disambiguationData":[TD([[makeQuery(id+"F0.imprint","IMPRINT",EDGE,{"derivedFrom":subQ0}),1.0]])]});}
            var Q167;
            {var subQ0=sQuery(id+"F0.wireOp",EDGE,"E369.6.0.0");Q167=makeQuery(id+"F0.imprint","IMPRINT",FACE,{"disambiguationData":[TD([[makeQuery(id+"F0.imprint","IMPRINT",EDGE,{"derivedFrom":subQ0}),1.0]])]});}
            var Q168;
            {var subQ0=sQuery(id+"F0.wireOp",EDGE,"E369.5.0.0");Q168=makeQuery(id+"F0.imprint","IMPRINT",FACE,{"disambiguationData":[TD([[makeQuery(id+"F0.imprint","IMPRINT",EDGE,{"derivedFrom":subQ0}),1.0]])]});}
            var Q169;
            {var subQ0=sQuery(id+"F0.wireOp",EDGE,"E369.4.0.0");Q169=makeQuery(id+"F0.imprint","IMPRINT",FACE,{"disambiguationData":[TD([[makeQuery(id+"F0.imprint","IMPRINT",EDGE,{"derivedFrom":subQ0}),1.0]])]});}
            var Q170;
            {var subQ0=sQuery(id+"F0.wireOp",EDGE,"E369.3.0.0");Q170=makeQuery(id+"F0.imprint","IMPRINT",FACE,{"disambiguationData":[TD([[makeQuery(id+"F0.imprint","IMPRINT",EDGE,{"derivedFrom":subQ0}),1.0]])]});}
            var Q171;
            {var subQ0=sQuery(id+"F0.wireOp",EDGE,"E369.2.0.0");Q171=makeQuery(id+"F0.imprint","IMPRINT",FACE,{"disambiguationData":[TD([[makeQuery(id+"F0.imprint","IMPRINT",EDGE,{"derivedFrom":subQ0}),1.0]])]});}
            var Q172;
            {var subQ0=sQuery(id+"F0.wireOp",EDGE,"E369.1.0.0");Q172=makeQuery(id+"F0.imprint","IMPRINT",FACE,{"disambiguationData":[TD([[makeQuery(id+"F0.imprint","IMPRINT",EDGE,{"derivedFrom":subQ0}),1.0]])]});}
            var Q173;
            {var subQ0=sQuery(id+"F0.wireOp",EDGE,"E359");Q173=makeQuery(id+"F0.imprint","IMPRINT",FACE,{"disambiguationData":[TD([[makeQuery(id+"F0.imprint","IMPRINT",EDGE,{"derivedFrom":subQ0}),1.0]])]});}
            var Q174;
            {var subQ2=sQuery(id+"F0.wireOp",EDGE,"E374.MirrorCS");Q174=makeQuery(id+"F0.imprint","IMPRINT",FACE,{"disambiguationData":[TD([[makeQuery(id+"F0.imprint","IMPRINT",EDGE,{"derivedFrom":subQ2}),-1.0]])]});}
            var Q175;
            {var subQ2=sQuery(id+"F0.wireOp",EDGE,"E374.MirrorCS");Q175=makeQuery(id+"F0.imprint","IMPRINT",FACE,{"disambiguationData":[TD([[makeQuery(id+"F0.imprint","IMPRINT",EDGE,{"derivedFrom":subQ2}),1.0]])]});}
            var Q176;
            {var subQ0=sQuery(id+"F0.wireOp",EDGE,"E384.MirrorCS");Q176=makeQuery(id+"F0.imprint","IMPRINT",FACE,{"disambiguationData":[TD([[makeQuery(id+"F0.imprint","IMPRINT",EDGE,{"derivedFrom":subQ0}),1.0]])]});}
            extrude(context, id + "F1", {"entities" : qUnion([Q0, Q1, Q2, Q3, Q4, Q5, Q6, Q7, Q8, Q9, Q10, Q11, Q12, Q13, Q14, Q15, Q16, Q17, Q18, Q19, Q20, Q21, Q22, Q23, Q24, Q25, Q26, Q27, Q28, Q29, Q30, Q31, Q32, Q33, Q34, Q35, Q36, Q37, Q38, Q39, Q40, Q41, Q42, Q43, Q44, Q45, Q46, Q47, Q48, Q49, Q50, Q51, Q52, Q53, Q54, Q55, Q56, Q57, Q58, Q59, Q60, Q61, Q62, Q63, Q64, Q65, Q66, Q67, Q68, Q69, Q70, Q71, Q72, Q73, Q74, Q75, Q76, Q77, Q78, Q79, Q80, Q81, Q82, Q83, Q84, Q85, Q86, Q87, Q88, Q89, Q90, Q91, Q92, Q93, Q94, Q95, Q96, Q97, Q98, Q99, Q100, Q101, Q102, Q103, Q104, Q105, Q106, Q107, Q108, Q109, Q110, Q111, Q112, Q113, Q114, Q115, Q116, Q117, Q118, Q119, Q120, Q121, Q122, Q123, Q124, Q125, Q126, Q127, Q128, Q129, Q130, Q131, Q132, Q133, Q134, Q135, Q136, Q137, Q138, Q139, Q140, Q141, Q142, Q143, Q144, Q145, Q146, Q147, Q148, Q149, Q150, Q151, Q152, Q153, Q154, Q155, Q156, Q157, Q158, Q159, Q160, Q161, Q162, Q163, Q164, Q165, Q166, Q167, Q168, Q169, Q170, Q171, Q172, Q173, Q174, Q175, Q176]), "depth" : 1.6 * mm});
        }
    });
